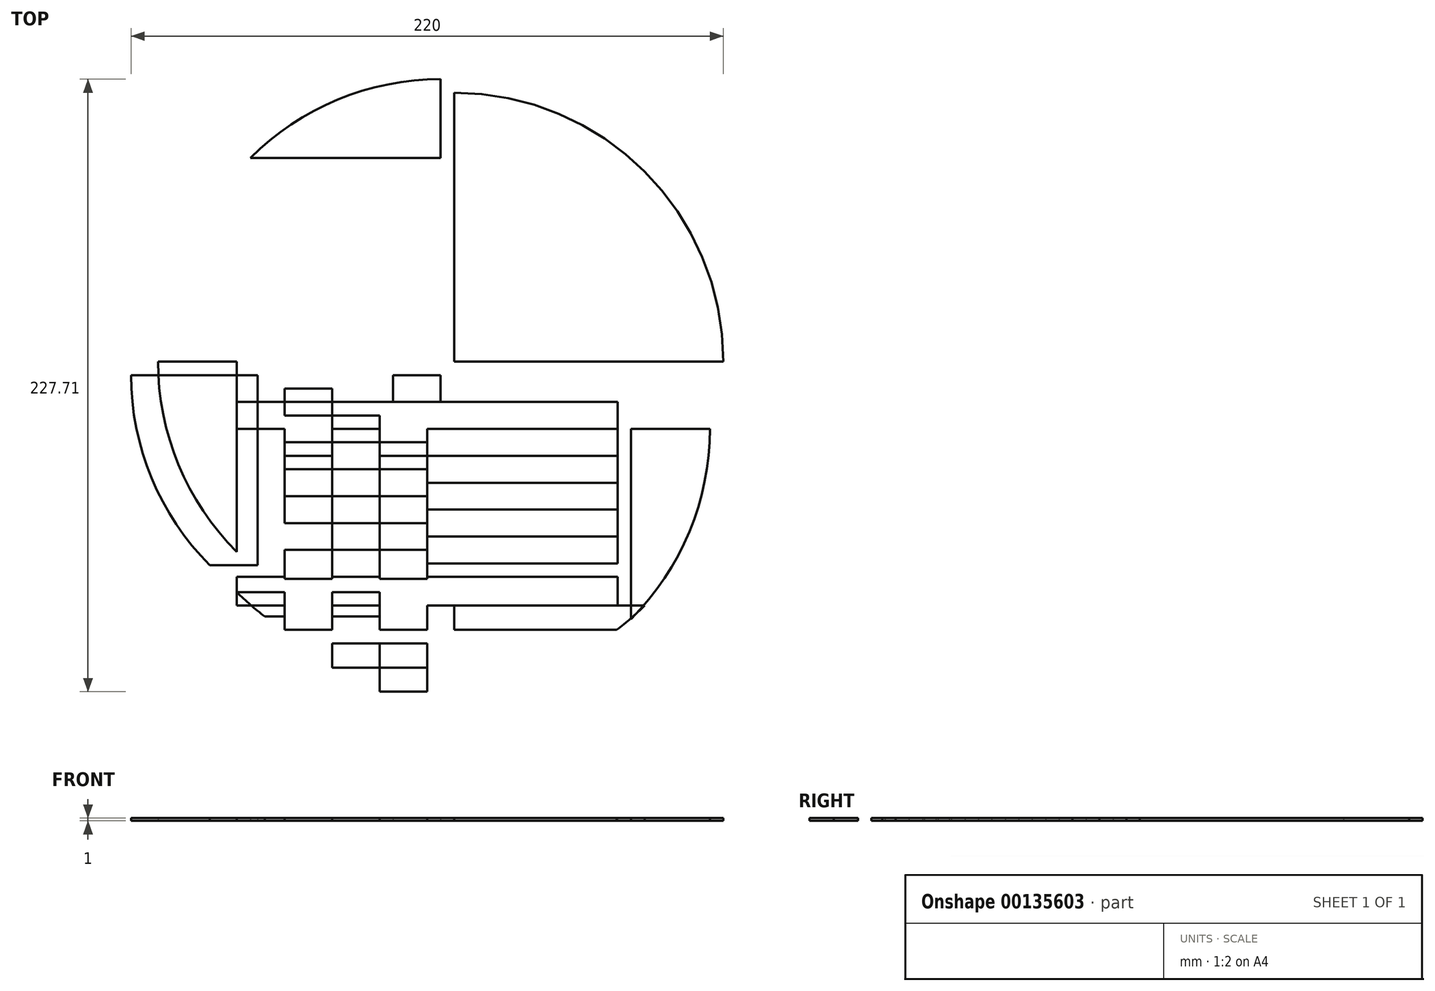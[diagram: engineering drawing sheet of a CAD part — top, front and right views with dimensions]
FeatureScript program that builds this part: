
annotation { "Feature Type Name" : "Feature", "Feature Type Description" : "" }
export const myFeature = defineFeature(function(context is Context, id is Id, definition is map)
    precondition{}
    {
        {
            assignVariable(context, id + "F0", {"name" : "d", "anyValue" : 5 * mm});
        }
        {
            var Q0;
            Q0=qCreatedBy(makeId("Top.planeOp"),FACE);
            var sketch = newSketch(context, id + "F1", { "sketchPlane" : qUnion([Q0])});
            skLineSegment(sketch, "E0.1", {"start": v(70.71, -70.71) * mm, "end": v(-70.71, -70.71) * mm});
            skLineSegment(sketch, "E0.2", {"start": v(-70.71, -70.71) * mm, "end": v(-70.71, 70.71) * mm});
            skLineSegment(sketch, "E1", {"start": v(70.71, 0) * mm, "end": v(-70.71, 0) * mm});
            skLineSegment(sketch, "E2", {"start": v(-14.1, -99) * mm, "end": v(14.1, -99) * mm});
            skArc(sketch, "E3", {"start": v(-14.1, -99) * mm, "mid": v(0, 100) * mm, "end": v(14.1, -99) * mm});
            skLineSegment(sketch, "E4", {"start": v(60.38, -79.71) * mm, "end": v(-60.38, -79.71) * mm});
            skLineSegment(sketch, "E5", {"start": v(46.16, -88.71) * mm, "end": v(-46.16, -88.71) * mm});
            skLineSegment(sketch, "E6", {"start": v(0, -70.71) * mm, "end": v(0, -99) * mm});
            skLineSegment(sketch, "E7", {"start": v(-70.71, 0) * mm, "end": v(-100, 0) * mm});
            skLineSegment(sketch, "E8", {"start": v(70.71, 0) * mm, "end": v(100, 0) * mm});
            skLineSegment(sketch, "E9", {"start": v(0, 70.71) * mm, "end": v(0, 100) * mm});
            skLineSegment(sketch, "E10", {"start": v(-70.71, -70.71) * mm, "end": v(-70.71, 0) * mm});
            skLineSegment(sketch, "E11", {"start": v(0, 70.71) * mm, "end": v(-70.71, 70.71) * mm});
            skLineSegment(sketch, "E12", {"start": v(70.71, 0) * mm, "end": v(70.71, -70.71) * mm});
            skLineSegment(sketch, "E13.0.1.0", {"start": v(70.71, -10) * mm, "end": v(-70.71, -10) * mm});
            skLineSegment(sketch, "E13.0.2.0", {"start": v(70.71, -20) * mm, "end": v(-70.71, -20) * mm});
            skLineSegment(sketch, "E13.0.3.0", {"start": v(70.71, -30) * mm, "end": v(-70.71, -30) * mm});
            skLineSegment(sketch, "E13.0.4.0", {"start": v(70.71, -40) * mm, "end": v(-70.71, -40) * mm});
            skLineSegment(sketch, "E13.0.5.0", {"start": v(70.71, -50) * mm, "end": v(-70.71, -50) * mm});
            skLineSegment(sketch, "E13.0.6.0", {"start": v(70.71, -60) * mm, "end": v(-70.71, -60) * mm});
            skLineSegment(sketch, "E13.direction1", {"start": v(-70.71, 0) * mm, "end": v(-45.71, 0) * mm, "construction": true});
            skLineSegment(sketch, "E13.direction2", {"start": v(-70.71, 0) * mm, "end": v(-70.71, -10) * mm, "construction": true});
            skLineSegment(sketch, "E14", {"start": v(0, 0) * mm, "end": v(0, 70.71) * mm});
            skLineSegment(sketch, "E15", {"start": v(0, 0) * mm, "end": v(0, -70.71) * mm});
            skLineSegment(sketch, "E16.1.0.0", {"start": v(-17.65, 0) * mm, "end": v(-17.65, -70.71) * mm});
            skLineSegment(sketch, "E16.2.0.0", {"start": v(-35.3, 0) * mm, "end": v(-35.3, -70.71) * mm});
            skLineSegment(sketch, "E16.3.0.0", {"start": v(-52.95, 0) * mm, "end": v(-52.95, -70.71) * mm});
            skLineSegment(sketch, "E16.direction1", {"start": v(0, -70.71) * mm, "end": v(-17.65, -70.71) * mm, "construction": true});
            skLineSegment(sketch, "E17", {"start": v(-35.3, -70.71) * mm, "end": v(-35.3, -88.71) * mm});
            skLineSegment(sketch, "E18", {"start": v(-52.95, -70.71) * mm, "end": v(-52.95, -79.71) * mm});
            skLineSegment(sketch, "E19", {"start": v(21.27, -97.71) * mm, "end": v(-21.27, -97.71) * mm});
            skLineSegment(sketch, "E20", {"start": v(-17.65, -70.71) * mm, "end": v(-17.65, -97.71) * mm});
            skSolve(sketch);
        }
        {
            var Q0;
            {var subQ0=sQuery(id+"F1.wireOp",EDGE,"E3");var subQ5=sQuery(id+"F1.wireOp",EDGE,"E4");var subQ6=makeQuery(id+"F1.imprint","INTERSECT",VERTEX,{"disambiguationData":[OD(0.0)],"derivedFrom":[subQ0,subQ5]});Q0=makeQuery(id+"F1.imprint","IMPRINT",FACE,{"disambiguationData":[TD([[makeQuery(id+"F1.imprint","IMPRINT",EDGE,{"disambiguationData":[TD([[subQ6,-1.0]])],"derivedFrom":subQ5}),-1.0]])]});}
            var Q1;
            {var subQ3=sQuery(id+"F1.wireOp",EDGE,"E18");Q1=makeQuery(id+"F1.imprint","IMPRINT",FACE,{"disambiguationData":[TD([[makeQuery(id+"F1.imprint","IMPRINT",EDGE,{"derivedFrom":subQ3}),-1.0]])]});}
            var Q2;
            {var subQ0=sQuery(id+"F1.wireOp",EDGE,"E20");var subQ5=sQuery(id+"F1.wireOp",EDGE,"E4");var subQ7=makeQuery(id+"F1.imprint","INTERSECT",VERTEX,{"derivedFrom":[subQ5,subQ0]});Q2=makeQuery(id+"F1.imprint","IMPRINT",FACE,{"disambiguationData":[TD([[makeQuery(id+"F1.imprint","IMPRINT",EDGE,{"disambiguationData":[TD([[subQ7,-1.0]])],"derivedFrom":subQ5}),-1.0]])]});}
            var Q3;
            {var subQ0=sQuery(id+"F1.wireOp",EDGE,"E15");var subQ5=sQuery(id+"F1.wireOp",EDGE,"E13.0.1.0");var subQ6=makeQuery(id+"F1.imprint","INTERSECT",VERTEX,{"derivedFrom":[subQ5,subQ0]});Q3=makeQuery(id+"F1.imprint","IMPRINT",FACE,{"disambiguationData":[TD([[makeQuery(id+"F1.imprint","IMPRINT",EDGE,{"disambiguationData":[TD([[subQ6,-1.0]])],"derivedFrom":subQ5}),-1.0]])]});}
            var Q4;
            {var subQ0=sQuery(id+"F1.wireOp",EDGE,"E16.2.0.0");var subQ1=sQuery(id+"F1.wireOp",EDGE,"E1");var subQ2=makeQuery(id+"F1.imprint","INTERSECT",VERTEX,{"derivedFrom":[subQ1,subQ0]});Q4=makeQuery(id+"F1.imprint","IMPRINT",FACE,{"disambiguationData":[TD([[makeQuery(id+"F1.imprint","IMPRINT",EDGE,{"disambiguationData":[TD([[subQ2,-1.0]])],"derivedFrom":subQ1}),1.0]])]});}
            var Q5;
            {var subQ0=sQuery(id+"F1.wireOp",EDGE,"E15");var subQ5=sQuery(id+"F1.wireOp",EDGE,"E13.0.1.0");var subQ6=makeQuery(id+"F1.imprint","INTERSECT",VERTEX,{"derivedFrom":[subQ5,subQ0]});Q5=makeQuery(id+"F1.imprint","IMPRINT",FACE,{"disambiguationData":[TD([[makeQuery(id+"F1.imprint","IMPRINT",EDGE,{"disambiguationData":[TD([[subQ6,-1.0]])],"derivedFrom":subQ5}),-1.0]])]});}
            var Q6;
            {var subQ0=sQuery(id+"F1.wireOp",EDGE,"E16.2.0.0");var subQ1=sQuery(id+"F1.wireOp",EDGE,"E1");var subQ2=makeQuery(id+"F1.imprint","INTERSECT",VERTEX,{"derivedFrom":[subQ1,subQ0]});Q6=makeQuery(id+"F1.imprint","IMPRINT",FACE,{"disambiguationData":[TD([[makeQuery(id+"F1.imprint","IMPRINT",EDGE,{"disambiguationData":[TD([[subQ2,-1.0]])],"derivedFrom":subQ1}),1.0]])]});}
            var Q7;
            {var subQ1=sQuery(id+"F1.wireOp",EDGE,"E8");Q7=makeQuery(id+"F1.imprint","IMPRINT",FACE,{"disambiguationData":[TD([[makeQuery(id+"F1.imprint","IMPRINT",EDGE,{"derivedFrom":subQ1}),1.0]])]});}
            var Q8;
            {var subQ0=sQuery(id+"F1.wireOp",EDGE,"E0.2");Q8=makeQuery(id+"F1.imprint","IMPRINT",FACE,{"disambiguationData":[TD([[makeQuery(id+"F1.imprint","IMPRINT",EDGE,{"derivedFrom":subQ0}),1.0]])]});}
            var Q9;
            {var subQ0=sQuery(id+"F1.wireOp",EDGE,"E15");var subQ5=sQuery(id+"F1.wireOp",EDGE,"E13.0.1.0");var subQ6=makeQuery(id+"F1.imprint","INTERSECT",VERTEX,{"derivedFrom":[subQ5,subQ0]});Q9=makeQuery(id+"F1.imprint","IMPRINT",FACE,{"disambiguationData":[TD([[makeQuery(id+"F1.imprint","IMPRINT",EDGE,{"disambiguationData":[TD([[subQ6,-1.0]])],"derivedFrom":subQ5}),-1.0]])]});}
            var Q10;
            {var subQ0=sQuery(id+"F1.wireOp",EDGE,"E16.2.0.0");var subQ1=sQuery(id+"F1.wireOp",EDGE,"E1");var subQ2=makeQuery(id+"F1.imprint","INTERSECT",VERTEX,{"derivedFrom":[subQ1,subQ0]});Q10=makeQuery(id+"F1.imprint","IMPRINT",FACE,{"disambiguationData":[TD([[makeQuery(id+"F1.imprint","IMPRINT",EDGE,{"disambiguationData":[TD([[subQ2,-1.0]])],"derivedFrom":subQ1}),1.0]])]});}
            var Q11;
            {var subQ0=sQuery(id+"F1.wireOp",EDGE,"E13.0.1.0");var subQ1=sQuery(id+"F1.wireOp",EDGE,"E10");var subQ2=makeQuery(id+"F1.imprint","INTERSECT",VERTEX,{"derivedFrom":[subQ1,subQ0]});Q11=makeQuery(id+"F1.imprint","IMPRINT",FACE,{"disambiguationData":[TD([[makeQuery(id+"F1.imprint","IMPRINT",EDGE,{"disambiguationData":[TD([[subQ2,1.0]])],"derivedFrom":subQ1}),-1.0]])]});}
            var Q12;
            {var subQ0=sQuery(id+"F1.wireOp",EDGE,"E16.2.0.0");var subQ1=sQuery(id+"F1.wireOp",EDGE,"E13.0.2.0");var subQ2=makeQuery(id+"F1.imprint","INTERSECT",VERTEX,{"derivedFrom":[subQ1,subQ0]});Q12=makeQuery(id+"F1.imprint","IMPRINT",FACE,{"disambiguationData":[TD([[makeQuery(id+"F1.imprint","IMPRINT",EDGE,{"disambiguationData":[TD([[subQ2,-1.0]])],"derivedFrom":subQ1}),1.0]])]});}
            var Q13;
            {var subQ0=sQuery(id+"F1.wireOp",EDGE,"E16.1.0.0");var subQ1=sQuery(id+"F1.wireOp",EDGE,"E13.0.1.0");var subQ2=makeQuery(id+"F1.imprint","INTERSECT",VERTEX,{"derivedFrom":[subQ1,subQ0]});Q13=makeQuery(id+"F1.imprint","IMPRINT",FACE,{"disambiguationData":[TD([[makeQuery(id+"F1.imprint","IMPRINT",EDGE,{"disambiguationData":[TD([[subQ2,-1.0]])],"derivedFrom":subQ1}),1.0]])]});}
            var Q14;
            {var subQ0=sQuery(id+"F1.wireOp",EDGE,"E15");var subQ1=sQuery(id+"F1.wireOp",EDGE,"E13.0.2.0");var subQ2=makeQuery(id+"F1.imprint","INTERSECT",VERTEX,{"derivedFrom":[subQ1,subQ0]});Q14=makeQuery(id+"F1.imprint","IMPRINT",FACE,{"disambiguationData":[TD([[makeQuery(id+"F1.imprint","IMPRINT",EDGE,{"disambiguationData":[TD([[subQ2,-1.0]])],"derivedFrom":subQ1}),1.0]])]});}
            var Q15;
            {var subQ0=sQuery(id+"F1.wireOp",EDGE,"E16.1.0.0");var subQ1=sQuery(id+"F1.wireOp",EDGE,"E13.0.3.0");var subQ2=makeQuery(id+"F1.imprint","INTERSECT",VERTEX,{"derivedFrom":[subQ1,subQ0]});Q15=makeQuery(id+"F1.imprint","IMPRINT",FACE,{"disambiguationData":[TD([[makeQuery(id+"F1.imprint","IMPRINT",EDGE,{"disambiguationData":[TD([[subQ2,-1.0]])],"derivedFrom":subQ1}),1.0]])]});}
            var Q16;
            {var subQ0=sQuery(id+"F1.wireOp",EDGE,"E13.0.3.0");var subQ1=sQuery(id+"F1.wireOp",EDGE,"E10");var subQ2=makeQuery(id+"F1.imprint","INTERSECT",VERTEX,{"derivedFrom":[subQ1,subQ0]});Q16=makeQuery(id+"F1.imprint","IMPRINT",FACE,{"disambiguationData":[TD([[makeQuery(id+"F1.imprint","IMPRINT",EDGE,{"disambiguationData":[TD([[subQ2,1.0]])],"derivedFrom":subQ1}),-1.0]])]});}
            var Q17;
            {var subQ0=sQuery(id+"F1.wireOp",EDGE,"E16.2.0.0");var subQ1=sQuery(id+"F1.wireOp",EDGE,"E13.0.4.0");var subQ2=makeQuery(id+"F1.imprint","INTERSECT",VERTEX,{"derivedFrom":[subQ1,subQ0]});Q17=makeQuery(id+"F1.imprint","IMPRINT",FACE,{"disambiguationData":[TD([[makeQuery(id+"F1.imprint","IMPRINT",EDGE,{"disambiguationData":[TD([[subQ2,-1.0]])],"derivedFrom":subQ1}),1.0]])]});}
            var Q18;
            {var subQ0=sQuery(id+"F1.wireOp",EDGE,"E15");var subQ1=sQuery(id+"F1.wireOp",EDGE,"E13.0.4.0");var subQ2=makeQuery(id+"F1.imprint","INTERSECT",VERTEX,{"derivedFrom":[subQ1,subQ0]});Q18=makeQuery(id+"F1.imprint","IMPRINT",FACE,{"disambiguationData":[TD([[makeQuery(id+"F1.imprint","IMPRINT",EDGE,{"disambiguationData":[TD([[subQ2,-1.0]])],"derivedFrom":subQ1}),1.0]])]});}
            var Q19;
            {var subQ0=sQuery(id+"F1.wireOp",EDGE,"E16.1.0.0");var subQ1=sQuery(id+"F1.wireOp",EDGE,"E13.0.5.0");var subQ2=makeQuery(id+"F1.imprint","INTERSECT",VERTEX,{"derivedFrom":[subQ1,subQ0]});Q19=makeQuery(id+"F1.imprint","IMPRINT",FACE,{"disambiguationData":[TD([[makeQuery(id+"F1.imprint","IMPRINT",EDGE,{"disambiguationData":[TD([[subQ2,-1.0]])],"derivedFrom":subQ1}),1.0]])]});}
            var Q20;
            {var subQ0=sQuery(id+"F1.wireOp",EDGE,"E16.2.0.0");var subQ5=sQuery(id+"F1.wireOp",EDGE,"E13.0.6.0");var subQ6=makeQuery(id+"F1.imprint","INTERSECT",VERTEX,{"derivedFrom":[subQ5,subQ0]});Q20=makeQuery(id+"F1.imprint","IMPRINT",FACE,{"disambiguationData":[TD([[makeQuery(id+"F1.imprint","IMPRINT",EDGE,{"disambiguationData":[TD([[subQ6,-1.0]])],"derivedFrom":subQ5}),1.0]])]});}
            var Q21;
            {var subQ0=sQuery(id+"F1.wireOp",EDGE,"E13.0.5.0");var subQ1=sQuery(id+"F1.wireOp",EDGE,"E10");var subQ2=makeQuery(id+"F1.imprint","INTERSECT",VERTEX,{"derivedFrom":[subQ1,subQ0]});Q21=makeQuery(id+"F1.imprint","IMPRINT",FACE,{"disambiguationData":[TD([[makeQuery(id+"F1.imprint","IMPRINT",EDGE,{"disambiguationData":[TD([[subQ2,1.0]])],"derivedFrom":subQ1}),-1.0]])]});}
            var Q22;
            {var subQ3=sQuery(id+"F1.wireOp",EDGE,"E18");Q22=makeQuery(id+"F1.imprint","IMPRINT",FACE,{"disambiguationData":[TD([[makeQuery(id+"F1.imprint","IMPRINT",EDGE,{"derivedFrom":subQ3}),-1.0]])]});}
            var Q23;
            {var subQ0=sQuery(id+"F1.wireOp",EDGE,"E13.0.1.0");var subQ1=sQuery(id+"F1.wireOp",EDGE,"E12");var subQ2=makeQuery(id+"F1.imprint","INTERSECT",VERTEX,{"derivedFrom":[subQ1,subQ0]});Q23=makeQuery(id+"F1.imprint","IMPRINT",FACE,{"disambiguationData":[TD([[makeQuery(id+"F1.imprint","IMPRINT",EDGE,{"disambiguationData":[TD([[subQ2,-1.0]])],"derivedFrom":subQ1}),-1.0]])]});}
            var Q24;
            {var subQ0=sQuery(id+"F1.wireOp",EDGE,"E13.0.3.0");var subQ1=sQuery(id+"F1.wireOp",EDGE,"E12");var subQ2=makeQuery(id+"F1.imprint","INTERSECT",VERTEX,{"derivedFrom":[subQ1,subQ0]});Q24=makeQuery(id+"F1.imprint","IMPRINT",FACE,{"disambiguationData":[TD([[makeQuery(id+"F1.imprint","IMPRINT",EDGE,{"disambiguationData":[TD([[subQ2,-1.0]])],"derivedFrom":subQ1}),-1.0]])]});}
            var Q25;
            {var subQ0=sQuery(id+"F1.wireOp",EDGE,"E13.0.5.0");var subQ1=sQuery(id+"F1.wireOp",EDGE,"E12");var subQ2=makeQuery(id+"F1.imprint","INTERSECT",VERTEX,{"derivedFrom":[subQ1,subQ0]});Q25=makeQuery(id+"F1.imprint","IMPRINT",FACE,{"disambiguationData":[TD([[makeQuery(id+"F1.imprint","IMPRINT",EDGE,{"disambiguationData":[TD([[subQ2,-1.0]])],"derivedFrom":subQ1}),-1.0]])]});}
            var Q26;
            {var subQ0=sQuery(id+"F1.wireOp",EDGE,"E15");var subQ5=sQuery(id+"F1.wireOp",EDGE,"E13.0.6.0");var subQ6=makeQuery(id+"F1.imprint","INTERSECT",VERTEX,{"derivedFrom":[subQ5,subQ0]});Q26=makeQuery(id+"F1.imprint","IMPRINT",FACE,{"disambiguationData":[TD([[makeQuery(id+"F1.imprint","IMPRINT",EDGE,{"disambiguationData":[TD([[subQ6,-1.0]])],"derivedFrom":subQ5}),1.0]])]});}
            var Q27;
            {var subQ0=sQuery(id+"F1.wireOp",EDGE,"E3");var subQ5=sQuery(id+"F1.wireOp",EDGE,"E4");var subQ6=makeQuery(id+"F1.imprint","INTERSECT",VERTEX,{"disambiguationData":[OD(0.0)],"derivedFrom":[subQ0,subQ5]});Q27=makeQuery(id+"F1.imprint","IMPRINT",FACE,{"disambiguationData":[TD([[makeQuery(id+"F1.imprint","IMPRINT",EDGE,{"disambiguationData":[TD([[subQ6,-1.0]])],"derivedFrom":subQ5}),-1.0]])]});}
            var Q28;
            {var subQ0=sQuery(id+"F1.wireOp",EDGE,"E6");var subQ1=sQuery(id+"F1.wireOp",EDGE,"E4");var subQ2=makeQuery(id+"F1.imprint","INTERSECT",VERTEX,{"derivedFrom":[subQ1,subQ0]});Q28=makeQuery(id+"F1.imprint","IMPRINT",FACE,{"disambiguationData":[TD([[makeQuery(id+"F1.imprint","IMPRINT",EDGE,{"disambiguationData":[TD([[subQ2,-1.0]])],"derivedFrom":subQ1}),1.0]])]});}
            var Q29;
            {var subQ1=sQuery(id+"F1.wireOp",EDGE,"E3");var subQ5=sQuery(id+"F1.wireOp",EDGE,"E5");var subQ6=makeQuery(id+"F1.imprint","INTERSECT",VERTEX,{"disambiguationData":[OD(1.0)],"derivedFrom":[subQ1,subQ5]});Q29=makeQuery(id+"F1.imprint","IMPRINT",FACE,{"disambiguationData":[TD([[makeQuery(id+"F1.imprint","IMPRINT",EDGE,{"disambiguationData":[TD([[subQ6,1.0]])],"derivedFrom":subQ1}),-1.0]])]});}
            var Q30;
            {var subQ0=sQuery(id+"F1.wireOp",EDGE,"E5");var subQ1=sQuery(id+"F1.wireOp",EDGE,"E3");var subQ2=makeQuery(id+"F1.imprint","INTERSECT",VERTEX,{"disambiguationData":[OD(0.0)],"derivedFrom":[subQ1,subQ0]});Q30=makeQuery(id+"F1.imprint","IMPRINT",FACE,{"disambiguationData":[TD([[makeQuery(id+"F1.imprint","IMPRINT",EDGE,{"disambiguationData":[TD([[subQ2,-1.0]])],"derivedFrom":subQ1}),-1.0]])]});}
            extrude(context, id + "F2", {"entities" : qUnion([Q0, Q1, Q2, Q3, Q4, Q5, Q6, Q7, Q8, Q9, Q10, Q11, Q12, Q13, Q14, Q15, Q16, Q17, Q18, Q19, Q20, Q21, Q22, Q23, Q24, Q25, Q26, Q27, Q28, Q29, Q30]), "depth" : 1 * mm});
        }
        {
            var Q0;
            {var subQ3=sQuery(id+"F1.wireOp",EDGE,"E8");Q0=makeQuery(id+"F1.imprint","IMPRINT",FACE,{"disambiguationData":[TD([[makeQuery(id+"F1.imprint","IMPRINT",EDGE,{"derivedFrom":subQ3}),-1.0]])]});}
            var Q1;
            {var subQ3=sQuery(id+"F1.wireOp",EDGE,"E7");Q1=makeQuery(id+"F1.imprint","IMPRINT",FACE,{"disambiguationData":[TD([[makeQuery(id+"F1.imprint","IMPRINT",EDGE,{"derivedFrom":subQ3}),1.0]])]});}
            var Q2;
            {var subQ5=sQuery(id+"F1.wireOp",EDGE,"E0.2");Q2=makeQuery(id+"F1.imprint","IMPRINT",FACE,{"disambiguationData":[TD([[makeQuery(id+"F1.imprint","IMPRINT",EDGE,{"derivedFrom":subQ5}),-1.0]])]});}
            var Q3;
            {var subQ1=sQuery(id+"F1.wireOp",EDGE,"E3");var subQ5=sQuery(id+"F1.wireOp",EDGE,"E4");var subQ6=makeQuery(id+"F1.imprint","INTERSECT",VERTEX,{"disambiguationData":[OD(1.0)],"derivedFrom":[subQ1,subQ5]});Q3=makeQuery(id+"F1.imprint","IMPRINT",FACE,{"disambiguationData":[TD([[makeQuery(id+"F1.imprint","IMPRINT",EDGE,{"disambiguationData":[TD([[subQ6,1.0]])],"derivedFrom":subQ1}),-1.0]])]});}
            var Q4;
            {var subQ1=sQuery(id+"F1.wireOp",EDGE,"E2");var subQ5=sQuery(id+"F1.wireOp",EDGE,"E3");var subQ6=makeQuery(id+"F1.imprint","INTERSECT",VERTEX,{"disambiguationData":[OD(0.0)],"derivedFrom":[subQ1,subQ5]});Q4=makeQuery(id+"F1.imprint","IMPRINT",FACE,{"disambiguationData":[TD([[makeQuery(id+"F1.imprint","IMPRINT",EDGE,{"disambiguationData":[TD([[subQ6,-1.0]])],"derivedFrom":subQ1}),1.0]])]});}
            extrude(context, id + "F3", {"entities" : qUnion([Q0, Q1, Q2, Q3, Q4]), "depth" : 1 * mm});
        }
        {
            var Q0;
            {var subQ0=sQuery(id+"F1.wireOp",EDGE,"E3");var subQ1=sQuery(id+"F1.wireOp",EDGE,"E2");var subQ2=makeQuery(id+"F1.imprint","INTERSECT",VERTEX,{"disambiguationData":[OD(1.0)],"derivedFrom":[subQ1,subQ0]});Q0=makeQuery(id+"F1.imprint","IMPRINT",FACE,{"disambiguationData":[TD([[makeQuery(id+"F1.imprint","IMPRINT",EDGE,{"disambiguationData":[TD([[subQ2,1.0]])],"derivedFrom":subQ1}),1.0]])]});}
            var Q1;
            {var subQ0=sQuery(id+"F1.wireOp",EDGE,"E6");var subQ1=sQuery(id+"F1.wireOp",EDGE,"E5");var subQ2=makeQuery(id+"F1.imprint","INTERSECT",VERTEX,{"derivedFrom":[subQ1,subQ0]});Q1=makeQuery(id+"F1.imprint","IMPRINT",FACE,{"disambiguationData":[TD([[makeQuery(id+"F1.imprint","IMPRINT",EDGE,{"disambiguationData":[TD([[subQ2,-1.0]])],"derivedFrom":subQ1}),1.0]])]});}
            var Q2;
            {var subQ0=sQuery(id+"F1.wireOp",EDGE,"E4");var subQ1=sQuery(id+"F1.wireOp",EDGE,"E3");var subQ2=makeQuery(id+"F1.imprint","INTERSECT",VERTEX,{"disambiguationData":[OD(0.0)],"derivedFrom":[subQ1,subQ0]});Q2=makeQuery(id+"F1.imprint","IMPRINT",FACE,{"disambiguationData":[TD([[makeQuery(id+"F1.imprint","IMPRINT",EDGE,{"disambiguationData":[TD([[subQ2,-1.0]])],"derivedFrom":subQ1}),-1.0]])]});}
            var Q3;
            {var subQ0=sQuery(id+"F1.wireOp",EDGE,"E20");var subQ1=sQuery(id+"F1.wireOp",EDGE,"E4");var subQ2=makeQuery(id+"F1.imprint","INTERSECT",VERTEX,{"derivedFrom":[subQ1,subQ0]});Q3=makeQuery(id+"F1.imprint","IMPRINT",FACE,{"disambiguationData":[TD([[makeQuery(id+"F1.imprint","IMPRINT",EDGE,{"disambiguationData":[TD([[subQ2,-1.0]])],"derivedFrom":subQ1}),1.0]])]});}
            var Q4;
            {var subQ0=sQuery(id+"F1.wireOp",EDGE,"E12");var subQ5=sQuery(id+"F1.wireOp",EDGE,"E13.0.6.0");var subQ6=makeQuery(id+"F1.imprint","INTERSECT",VERTEX,{"derivedFrom":[subQ0,subQ5]});Q4=makeQuery(id+"F1.imprint","IMPRINT",FACE,{"disambiguationData":[TD([[makeQuery(id+"F1.imprint","IMPRINT",EDGE,{"disambiguationData":[TD([[subQ6,-1.0]])],"derivedFrom":subQ5}),1.0]])]});}
            var Q5;
            {var subQ0=sQuery(id+"F1.wireOp",EDGE,"E6");var subQ5=sQuery(id+"F1.wireOp",EDGE,"E4");var subQ6=makeQuery(id+"F1.imprint","INTERSECT",VERTEX,{"derivedFrom":[subQ5,subQ0]});Q5=makeQuery(id+"F1.imprint","IMPRINT",FACE,{"disambiguationData":[TD([[makeQuery(id+"F1.imprint","IMPRINT",EDGE,{"disambiguationData":[TD([[subQ6,-1.0]])],"derivedFrom":subQ5}),-1.0]])]});}
            var Q6;
            {var subQ0=sQuery(id+"F1.wireOp",EDGE,"E15");var subQ1=sQuery(id+"F1.wireOp",EDGE,"E13.0.5.0");var subQ2=makeQuery(id+"F1.imprint","INTERSECT",VERTEX,{"derivedFrom":[subQ1,subQ0]});Q6=makeQuery(id+"F1.imprint","IMPRINT",FACE,{"disambiguationData":[TD([[makeQuery(id+"F1.imprint","IMPRINT",EDGE,{"disambiguationData":[TD([[subQ2,-1.0]])],"derivedFrom":subQ1}),1.0]])]});}
            var Q7;
            {var subQ3=sQuery(id+"F1.wireOp",EDGE,"E18");Q7=makeQuery(id+"F1.imprint","IMPRINT",FACE,{"disambiguationData":[TD([[makeQuery(id+"F1.imprint","IMPRINT",EDGE,{"derivedFrom":subQ3}),1.0]])]});}
            var Q8;
            {var subQ0=sQuery(id+"F1.wireOp",EDGE,"E16.1.0.0");var subQ5=sQuery(id+"F1.wireOp",EDGE,"E13.0.6.0");var subQ6=makeQuery(id+"F1.imprint","INTERSECT",VERTEX,{"derivedFrom":[subQ5,subQ0]});Q8=makeQuery(id+"F1.imprint","IMPRINT",FACE,{"disambiguationData":[TD([[makeQuery(id+"F1.imprint","IMPRINT",EDGE,{"disambiguationData":[TD([[subQ6,-1.0]])],"derivedFrom":subQ5}),1.0]])]});}
            var Q9;
            {var subQ0=sQuery(id+"F1.wireOp",EDGE,"E10");var subQ5=sQuery(id+"F1.wireOp",EDGE,"E13.0.6.0");var subQ6=makeQuery(id+"F1.imprint","INTERSECT",VERTEX,{"derivedFrom":[subQ0,subQ5]});Q9=makeQuery(id+"F1.imprint","IMPRINT",FACE,{"disambiguationData":[TD([[makeQuery(id+"F1.imprint","IMPRINT",EDGE,{"disambiguationData":[TD([[subQ6,1.0]])],"derivedFrom":subQ5}),1.0]])]});}
            var Q10;
            {var subQ0=sQuery(id+"F1.wireOp",EDGE,"E16.2.0.0");var subQ1=sQuery(id+"F1.wireOp",EDGE,"E13.0.5.0");var subQ2=makeQuery(id+"F1.imprint","INTERSECT",VERTEX,{"derivedFrom":[subQ1,subQ0]});Q10=makeQuery(id+"F1.imprint","IMPRINT",FACE,{"disambiguationData":[TD([[makeQuery(id+"F1.imprint","IMPRINT",EDGE,{"disambiguationData":[TD([[subQ2,-1.0]])],"derivedFrom":subQ1}),1.0]])]});}
            var Q11;
            {var subQ0=sQuery(id+"F1.wireOp",EDGE,"E13.0.4.0");var subQ1=sQuery(id+"F1.wireOp",EDGE,"E10");var subQ2=makeQuery(id+"F1.imprint","INTERSECT",VERTEX,{"derivedFrom":[subQ1,subQ0]});Q11=makeQuery(id+"F1.imprint","IMPRINT",FACE,{"disambiguationData":[TD([[makeQuery(id+"F1.imprint","IMPRINT",EDGE,{"disambiguationData":[TD([[subQ2,1.0]])],"derivedFrom":subQ1}),-1.0]])]});}
            var Q12;
            {var subQ0=sQuery(id+"F1.wireOp",EDGE,"E16.1.0.0");var subQ1=sQuery(id+"F1.wireOp",EDGE,"E13.0.4.0");var subQ2=makeQuery(id+"F1.imprint","INTERSECT",VERTEX,{"derivedFrom":[subQ1,subQ0]});Q12=makeQuery(id+"F1.imprint","IMPRINT",FACE,{"disambiguationData":[TD([[makeQuery(id+"F1.imprint","IMPRINT",EDGE,{"disambiguationData":[TD([[subQ2,-1.0]])],"derivedFrom":subQ1}),1.0]])]});}
            var Q13;
            {var subQ0=sQuery(id+"F1.wireOp",EDGE,"E16.2.0.0");var subQ1=sQuery(id+"F1.wireOp",EDGE,"E13.0.3.0");var subQ2=makeQuery(id+"F1.imprint","INTERSECT",VERTEX,{"derivedFrom":[subQ1,subQ0]});Q13=makeQuery(id+"F1.imprint","IMPRINT",FACE,{"disambiguationData":[TD([[makeQuery(id+"F1.imprint","IMPRINT",EDGE,{"disambiguationData":[TD([[subQ2,-1.0]])],"derivedFrom":subQ1}),1.0]])]});}
            var Q14;
            {var subQ0=sQuery(id+"F1.wireOp",EDGE,"E16.1.0.0");var subQ1=sQuery(id+"F1.wireOp",EDGE,"E13.0.2.0");var subQ2=makeQuery(id+"F1.imprint","INTERSECT",VERTEX,{"derivedFrom":[subQ1,subQ0]});Q14=makeQuery(id+"F1.imprint","IMPRINT",FACE,{"disambiguationData":[TD([[makeQuery(id+"F1.imprint","IMPRINT",EDGE,{"disambiguationData":[TD([[subQ2,-1.0]])],"derivedFrom":subQ1}),1.0]])]});}
            var Q15;
            {var subQ0=sQuery(id+"F1.wireOp",EDGE,"E15");var subQ1=sQuery(id+"F1.wireOp",EDGE,"E13.0.3.0");var subQ2=makeQuery(id+"F1.imprint","INTERSECT",VERTEX,{"derivedFrom":[subQ1,subQ0]});Q15=makeQuery(id+"F1.imprint","IMPRINT",FACE,{"disambiguationData":[TD([[makeQuery(id+"F1.imprint","IMPRINT",EDGE,{"disambiguationData":[TD([[subQ2,-1.0]])],"derivedFrom":subQ1}),1.0]])]});}
            var Q16;
            {var subQ0=sQuery(id+"F1.wireOp",EDGE,"E15");var subQ1=sQuery(id+"F1.wireOp",EDGE,"E13.0.1.0");var subQ2=makeQuery(id+"F1.imprint","INTERSECT",VERTEX,{"derivedFrom":[subQ1,subQ0]});Q16=makeQuery(id+"F1.imprint","IMPRINT",FACE,{"disambiguationData":[TD([[makeQuery(id+"F1.imprint","IMPRINT",EDGE,{"disambiguationData":[TD([[subQ2,-1.0]])],"derivedFrom":subQ1}),1.0]])]});}
            var Q17;
            {var subQ0=sQuery(id+"F1.wireOp",EDGE,"E16.1.0.0");var subQ1=sQuery(id+"F1.wireOp",EDGE,"E1");var subQ2=makeQuery(id+"F1.imprint","INTERSECT",VERTEX,{"derivedFrom":[subQ1,subQ0]});Q17=makeQuery(id+"F1.imprint","IMPRINT",FACE,{"disambiguationData":[TD([[makeQuery(id+"F1.imprint","IMPRINT",EDGE,{"disambiguationData":[TD([[subQ2,-1.0]])],"derivedFrom":subQ1}),1.0]])]});}
            var Q18;
            {var subQ0=sQuery(id+"F1.wireOp",EDGE,"E16.2.0.0");var subQ1=sQuery(id+"F1.wireOp",EDGE,"E13.0.1.0");var subQ2=makeQuery(id+"F1.imprint","INTERSECT",VERTEX,{"derivedFrom":[subQ1,subQ0]});Q18=makeQuery(id+"F1.imprint","IMPRINT",FACE,{"disambiguationData":[TD([[makeQuery(id+"F1.imprint","IMPRINT",EDGE,{"disambiguationData":[TD([[subQ2,-1.0]])],"derivedFrom":subQ1}),1.0]])]});}
            var Q19;
            {var subQ0=sQuery(id+"F1.wireOp",EDGE,"E13.0.2.0");var subQ1=sQuery(id+"F1.wireOp",EDGE,"E10");var subQ2=makeQuery(id+"F1.imprint","INTERSECT",VERTEX,{"derivedFrom":[subQ1,subQ0]});Q19=makeQuery(id+"F1.imprint","IMPRINT",FACE,{"disambiguationData":[TD([[makeQuery(id+"F1.imprint","IMPRINT",EDGE,{"disambiguationData":[TD([[subQ2,1.0]])],"derivedFrom":subQ1}),-1.0]])]});}
            var Q20;
            {var subQ0=sQuery(id+"F1.wireOp",EDGE,"E10");var subQ5=sQuery(id+"F1.wireOp",EDGE,"E13.0.1.0");var subQ6=makeQuery(id+"F1.imprint","INTERSECT",VERTEX,{"derivedFrom":[subQ0,subQ5]});Q20=makeQuery(id+"F1.imprint","IMPRINT",FACE,{"disambiguationData":[TD([[makeQuery(id+"F1.imprint","IMPRINT",EDGE,{"disambiguationData":[TD([[subQ6,1.0]])],"derivedFrom":subQ5}),-1.0]])]});}
            var Q21;
            {var subQ0=sQuery(id+"F1.wireOp",EDGE,"E12");var subQ5=sQuery(id+"F1.wireOp",EDGE,"E13.0.1.0");var subQ6=makeQuery(id+"F1.imprint","INTERSECT",VERTEX,{"derivedFrom":[subQ0,subQ5]});Q21=makeQuery(id+"F1.imprint","IMPRINT",FACE,{"disambiguationData":[TD([[makeQuery(id+"F1.imprint","IMPRINT",EDGE,{"disambiguationData":[TD([[subQ6,-1.0]])],"derivedFrom":subQ5}),-1.0]])]});}
            var Q22;
            {var subQ0=sQuery(id+"F1.wireOp",EDGE,"E13.0.2.0");var subQ1=sQuery(id+"F1.wireOp",EDGE,"E12");var subQ2=makeQuery(id+"F1.imprint","INTERSECT",VERTEX,{"derivedFrom":[subQ1,subQ0]});Q22=makeQuery(id+"F1.imprint","IMPRINT",FACE,{"disambiguationData":[TD([[makeQuery(id+"F1.imprint","IMPRINT",EDGE,{"disambiguationData":[TD([[subQ2,-1.0]])],"derivedFrom":subQ1}),-1.0]])]});}
            var Q23;
            {var subQ0=sQuery(id+"F1.wireOp",EDGE,"E13.0.4.0");var subQ1=sQuery(id+"F1.wireOp",EDGE,"E12");var subQ2=makeQuery(id+"F1.imprint","INTERSECT",VERTEX,{"derivedFrom":[subQ1,subQ0]});Q23=makeQuery(id+"F1.imprint","IMPRINT",FACE,{"disambiguationData":[TD([[makeQuery(id+"F1.imprint","IMPRINT",EDGE,{"disambiguationData":[TD([[subQ2,-1.0]])],"derivedFrom":subQ1}),-1.0]])]});}
            var Q24;
            {var subQ2=sQuery(id+"F1.wireOp",EDGE,"E9");Q24=makeQuery(id+"F1.imprint","IMPRINT",FACE,{"disambiguationData":[TD([[makeQuery(id+"F1.imprint","IMPRINT",EDGE,{"derivedFrom":subQ2}),1.0]])]});}
            extrude(context, id + "F4", {"entities" : qUnion([Q0, Q1, Q2, Q3, Q4, Q5, Q6, Q7, Q8, Q9, Q10, Q11, Q12, Q13, Q14, Q15, Q16, Q17, Q18, Q19, Q20, Q21, Q22, Q23, Q24]), "depth" : 1 * mm});
        }
        {
            var Q0;
            Q0=makeQuery(id+"F3.opExtrude","SWEPT_BODY",BODY,{"disambiguationData":[OSD([sQuery(id+"F1.wireOp",EDGE,"E0.2"),sQuery(id+"F1.wireOp",EDGE,"E1"),sQuery(id+"F1.wireOp",EDGE,"E11"),sQuery(id+"F1.wireOp",EDGE,"E14")])]});
            var Q1;
            Q1=makeQuery(id+"F2.opExtrude","SWEPT_BODY",BODY,{"disambiguationData":[OSD([sQuery(id+"F1.wireOp",EDGE,"E0.2"),sQuery(id+"F1.wireOp",EDGE,"E3"),sQuery(id+"F1.wireOp",EDGE,"E7")])]});
            var Q2;
            Q2=makeQuery(id+"F4.opExtrude","SWEPT_BODY",BODY,{"disambiguationData":[OSD([sQuery(id+"F1.wireOp",EDGE,"E3"),sQuery(id+"F1.wireOp",EDGE,"E9"),sQuery(id+"F1.wireOp",EDGE,"E11")])]});
            var Q3;
            Q3=sQuery(id+"F1.wireOp",EDGE,"Lgyj7vdr-Zl23-fVqB-5WY6-XuLikOYo5ZJ7");
            transform(context, id + "F5", {"entities" : qUnion([Q0, Q1, Q2]), "transformType" : TransformType.TRANSLATION_3D, "dx" : -getVariable(context, 'd'), "dy" : 0 * mm, "dz" : 0 * mm, "makeCopy" : false});
        }
        {
            var Q0;
            Q0=makeQuery(id+"F2.opExtrude","SWEPT_BODY",BODY,{"disambiguationData":[OSD([sQuery(id+"F1.wireOp",EDGE,"E1"),sQuery(id+"F1.wireOp",EDGE,"E13.0.1.0"),sQuery(id+"F1.wireOp",EDGE,"E15"),sQuery(id+"F1.wireOp",EDGE,"E16.1.0.0")])]});
            var Q1;
            Q1=makeQuery(id+"F2.opExtrude","SWEPT_BODY",BODY,{"disambiguationData":[OSD([sQuery(id+"F1.wireOp",EDGE,"E1"),sQuery(id+"F1.wireOp",EDGE,"E13.0.1.0"),sQuery(id+"F1.wireOp",EDGE,"E16.2.0.0"),sQuery(id+"F1.wireOp",EDGE,"E16.3.0.0")])]});
            var Q2;
            Q2=makeQuery(id+"F3.opExtrude","SWEPT_BODY",BODY,{"disambiguationData":[OSD([sQuery(id+"F1.wireOp",EDGE,"E3"),sQuery(id+"F1.wireOp",EDGE,"E7"),sQuery(id+"F1.wireOp",EDGE,"E10")])]});
            var Q3;
            Q3=makeQuery(id+"F3.opExtrude","SWEPT_BODY",BODY,{"disambiguationData":[OSD([sQuery(id+"F1.wireOp",EDGE,"E3"),sQuery(id+"F1.wireOp",EDGE,"E4"),sQuery(id+"F1.wireOp",EDGE,"E5"),sQuery(id+"F1.wireOp",EDGE,"E17")])]});
            var Q4;
            Q4=makeQuery(id+"F2.opExtrude","SWEPT_BODY",BODY,{"disambiguationData":[OSD([sQuery(id+"F1.wireOp",EDGE,"E13.0.3.0"),sQuery(id+"F1.wireOp",EDGE,"E13.0.4.0"),sQuery(id+"F1.wireOp",EDGE,"E16.1.0.0"),sQuery(id+"F1.wireOp",EDGE,"E16.2.0.0")])]});
            var Q5;
            Q5=makeQuery(id+"F2.opExtrude","SWEPT_BODY",BODY,{"disambiguationData":[OSD([sQuery(id+"F1.wireOp",EDGE,"E13.0.4.0"),sQuery(id+"F1.wireOp",EDGE,"E13.0.5.0"),sQuery(id+"F1.wireOp",EDGE,"E15"),sQuery(id+"F1.wireOp",EDGE,"E16.1.0.0")])]});
            var Q6;
            Q6=makeQuery(id+"F2.opExtrude","SWEPT_BODY",BODY,{"disambiguationData":[OSD([sQuery(id+"F1.wireOp",EDGE,"E13.0.4.0"),sQuery(id+"F1.wireOp",EDGE,"E13.0.5.0"),sQuery(id+"F1.wireOp",EDGE,"E16.2.0.0"),sQuery(id+"F1.wireOp",EDGE,"E16.3.0.0")])]});
            var Q7;
            Q7=makeQuery(id+"F2.opExtrude","SWEPT_BODY",BODY,{"disambiguationData":[OSD([sQuery(id+"F1.wireOp",EDGE,"E13.0.5.0"),sQuery(id+"F1.wireOp",EDGE,"E13.0.6.0"),sQuery(id+"F1.wireOp",EDGE,"E16.1.0.0"),sQuery(id+"F1.wireOp",EDGE,"E16.2.0.0")])]});
            var Q8;
            Q8=makeQuery(id+"F2.opExtrude","SWEPT_BODY",BODY,{"disambiguationData":[OSD([sQuery(id+"F1.wireOp",EDGE,"E3"),sQuery(id+"F1.wireOp",EDGE,"E5"),sQuery(id+"F1.wireOp",EDGE,"E19"),sQuery(id+"F1.wireOp",EDGE,"E20")])]});
            var Q9;
            Q9=makeQuery(id+"F3.opExtrude","SWEPT_BODY",BODY,{"disambiguationData":[OSD([sQuery(id+"F1.wireOp",EDGE,"E2"),sQuery(id+"F1.wireOp",EDGE,"E3"),sQuery(id+"F1.wireOp",EDGE,"E6"),sQuery(id+"F1.wireOp",EDGE,"E19")])]});
            var Q10;
            Q10=makeQuery(id+"F4.opExtrude","SWEPT_BODY",BODY,{"disambiguationData":[OSD([sQuery(id+"F1.wireOp",EDGE,"E10"),sQuery(id+"F1.wireOp",EDGE,"E13.0.4.0"),sQuery(id+"F1.wireOp",EDGE,"E13.0.5.0"),sQuery(id+"F1.wireOp",EDGE,"E16.3.0.0")])]});
            var Q11;
            Q11=makeQuery(id+"F4.opExtrude","SWEPT_BODY",BODY,{"disambiguationData":[OSD([sQuery(id+"F1.wireOp",EDGE,"E13.0.5.0"),sQuery(id+"F1.wireOp",EDGE,"E13.0.6.0"),sQuery(id+"F1.wireOp",EDGE,"E16.2.0.0"),sQuery(id+"F1.wireOp",EDGE,"E16.3.0.0")])]});
            var Q12;
            Q12=makeQuery(id+"F4.opExtrude","SWEPT_BODY",BODY,{"disambiguationData":[OSD([sQuery(id+"F1.wireOp",EDGE,"E13.0.5.0"),sQuery(id+"F1.wireOp",EDGE,"E13.0.6.0"),sQuery(id+"F1.wireOp",EDGE,"E15"),sQuery(id+"F1.wireOp",EDGE,"E16.1.0.0")])]});
            var Q13;
            Q13=makeQuery(id+"F4.opExtrude","SWEPT_BODY",BODY,{"disambiguationData":[OSD([sQuery(id+"F1.wireOp",EDGE,"E13.0.4.0"),sQuery(id+"F1.wireOp",EDGE,"E13.0.5.0"),sQuery(id+"F1.wireOp",EDGE,"E16.1.0.0"),sQuery(id+"F1.wireOp",EDGE,"E16.2.0.0")])]});
            var Q14;
            Q14=makeQuery(id+"F4.opExtrude","SWEPT_BODY",BODY,{"disambiguationData":[OSD([sQuery(id+"F1.wireOp",EDGE,"E13.0.3.0"),sQuery(id+"F1.wireOp",EDGE,"E13.0.4.0"),sQuery(id+"F1.wireOp",EDGE,"E16.2.0.0"),sQuery(id+"F1.wireOp",EDGE,"E16.3.0.0")])]});
            var Q15;
            Q15=makeQuery(id+"F4.opExtrude","SWEPT_BODY",BODY,{"disambiguationData":[OSD([sQuery(id+"F1.wireOp",EDGE,"E13.0.3.0"),sQuery(id+"F1.wireOp",EDGE,"E13.0.4.0"),sQuery(id+"F1.wireOp",EDGE,"E15"),sQuery(id+"F1.wireOp",EDGE,"E16.1.0.0")])]});
            var Q16;
            Q16=makeQuery(id+"F4.opExtrude","SWEPT_BODY",BODY,{"disambiguationData":[OSD([sQuery(id+"F1.wireOp",EDGE,"E13.0.2.0"),sQuery(id+"F1.wireOp",EDGE,"E13.0.3.0"),sQuery(id+"F1.wireOp",EDGE,"E16.1.0.0"),sQuery(id+"F1.wireOp",EDGE,"E16.2.0.0")])]});
            var Q17;
            Q17=makeQuery(id+"F4.opExtrude","SWEPT_BODY",BODY,{"disambiguationData":[OSD([sQuery(id+"F1.wireOp",EDGE,"E13.0.1.0"),sQuery(id+"F1.wireOp",EDGE,"E13.0.2.0"),sQuery(id+"F1.wireOp",EDGE,"E16.2.0.0"),sQuery(id+"F1.wireOp",EDGE,"E16.3.0.0")])]});
            var Q18;
            Q18=makeQuery(id+"F4.opExtrude","SWEPT_BODY",BODY,{"disambiguationData":[OSD([sQuery(id+"F1.wireOp",EDGE,"E13.0.1.0"),sQuery(id+"F1.wireOp",EDGE,"E13.0.2.0"),sQuery(id+"F1.wireOp",EDGE,"E15"),sQuery(id+"F1.wireOp",EDGE,"E16.1.0.0")])]});
            var Q19;
            Q19=makeQuery(id+"F4.opExtrude","SWEPT_BODY",BODY,{"disambiguationData":[OSD([sQuery(id+"F1.wireOp",EDGE,"E5"),sQuery(id+"F1.wireOp",EDGE,"E6"),sQuery(id+"F1.wireOp",EDGE,"E19"),sQuery(id+"F1.wireOp",EDGE,"E20")])]});
            var Q20;
            Q20=makeQuery(id+"F4.opExtrude","SWEPT_BODY",BODY,{"disambiguationData":[OSD([sQuery(id+"F1.wireOp",EDGE,"E10"),sQuery(id+"F1.wireOp",EDGE,"E13.0.2.0"),sQuery(id+"F1.wireOp",EDGE,"E13.0.3.0"),sQuery(id+"F1.wireOp",EDGE,"E16.3.0.0")])]});
            var Q21;
            Q21=makeQuery(id+"F4.opExtrude","SWEPT_BODY",BODY,{"disambiguationData":[OSD([sQuery(id+"F1.wireOp",EDGE,"E4"),sQuery(id+"F1.wireOp",EDGE,"E5"),sQuery(id+"F1.wireOp",EDGE,"E17"),sQuery(id+"F1.wireOp",EDGE,"E20")])]});
            var Q22;
            Q22=makeQuery(id+"F4.opExtrude","SWEPT_BODY",BODY,{"disambiguationData":[OSD([sQuery(id+"F1.wireOp",EDGE,"E1"),sQuery(id+"F1.wireOp",EDGE,"E10"),sQuery(id+"F1.wireOp",EDGE,"E13.0.1.0"),sQuery(id+"F1.wireOp",EDGE,"E16.3.0.0")])]});
            var Q23;
            Q23=makeQuery(id+"F4.opExtrude","SWEPT_BODY",BODY,{"disambiguationData":[OSD([sQuery(id+"F1.wireOp",EDGE,"E1"),sQuery(id+"F1.wireOp",EDGE,"E13.0.1.0"),sQuery(id+"F1.wireOp",EDGE,"E16.1.0.0"),sQuery(id+"F1.wireOp",EDGE,"E16.2.0.0")])]});
            var Q24;
            Q24=makeQuery(id+"F4.opExtrude","SWEPT_BODY",BODY,{"disambiguationData":[OSD([sQuery(id+"F1.wireOp",EDGE,"E0.1"),sQuery(id+"F1.wireOp",EDGE,"E10"),sQuery(id+"F1.wireOp",EDGE,"E13.0.6.0"),sQuery(id+"F1.wireOp",EDGE,"E16.3.0.0")])]});
            var Q25;
            Q25=makeQuery(id+"F4.opExtrude","SWEPT_BODY",BODY,{"disambiguationData":[OSD([sQuery(id+"F1.wireOp",EDGE,"E0.1"),sQuery(id+"F1.wireOp",EDGE,"E4"),sQuery(id+"F1.wireOp",EDGE,"E17"),sQuery(id+"F1.wireOp",EDGE,"E18")])]});
            var Q26;
            Q26=makeQuery(id+"F4.opExtrude","SWEPT_BODY",BODY,{"disambiguationData":[OSD([sQuery(id+"F1.wireOp",EDGE,"E0.1"),sQuery(id+"F1.wireOp",EDGE,"E4"),sQuery(id+"F1.wireOp",EDGE,"E6"),sQuery(id+"F1.wireOp",EDGE,"E20")])]});
            var Q27;
            Q27=makeQuery(id+"F4.opExtrude","SWEPT_BODY",BODY,{"disambiguationData":[OSD([sQuery(id+"F1.wireOp",EDGE,"E0.1"),sQuery(id+"F1.wireOp",EDGE,"E13.0.6.0"),sQuery(id+"F1.wireOp",EDGE,"E16.1.0.0"),sQuery(id+"F1.wireOp",EDGE,"E16.2.0.0")])]});
            var Q28;
            Q28=makeQuery(id+"F2.opExtrude","SWEPT_BODY",BODY,{"disambiguationData":[OSD([sQuery(id+"F1.wireOp",EDGE,"E13.0.2.0"),sQuery(id+"F1.wireOp",EDGE,"E13.0.3.0"),sQuery(id+"F1.wireOp",EDGE,"E16.2.0.0"),sQuery(id+"F1.wireOp",EDGE,"E16.3.0.0")])]});
            var Q29;
            Q29=makeQuery(id+"F2.opExtrude","SWEPT_BODY",BODY,{"disambiguationData":[OSD([sQuery(id+"F1.wireOp",EDGE,"E13.0.2.0"),sQuery(id+"F1.wireOp",EDGE,"E13.0.3.0"),sQuery(id+"F1.wireOp",EDGE,"E15"),sQuery(id+"F1.wireOp",EDGE,"E16.1.0.0")])]});
            var Q30;
            Q30=makeQuery(id+"F2.opExtrude","SWEPT_BODY",BODY,{"disambiguationData":[OSD([sQuery(id+"F1.wireOp",EDGE,"E13.0.1.0"),sQuery(id+"F1.wireOp",EDGE,"E13.0.2.0"),sQuery(id+"F1.wireOp",EDGE,"E16.1.0.0"),sQuery(id+"F1.wireOp",EDGE,"E16.2.0.0")])]});
            var Q31;
            Q31=makeQuery(id+"F2.opExtrude","SWEPT_BODY",BODY,{"disambiguationData":[OSD([sQuery(id+"F1.wireOp",EDGE,"E10"),sQuery(id+"F1.wireOp",EDGE,"E13.0.1.0"),sQuery(id+"F1.wireOp",EDGE,"E13.0.2.0"),sQuery(id+"F1.wireOp",EDGE,"E16.3.0.0")])]});
            var Q32;
            Q32=makeQuery(id+"F2.opExtrude","SWEPT_BODY",BODY,{"disambiguationData":[OSD([sQuery(id+"F1.wireOp",EDGE,"E10"),sQuery(id+"F1.wireOp",EDGE,"E13.0.3.0"),sQuery(id+"F1.wireOp",EDGE,"E13.0.4.0"),sQuery(id+"F1.wireOp",EDGE,"E16.3.0.0")])]});
            var Q33;
            Q33=makeQuery(id+"F2.opExtrude","SWEPT_BODY",BODY,{"disambiguationData":[OSD([sQuery(id+"F1.wireOp",EDGE,"E10"),sQuery(id+"F1.wireOp",EDGE,"E13.0.5.0"),sQuery(id+"F1.wireOp",EDGE,"E13.0.6.0"),sQuery(id+"F1.wireOp",EDGE,"E16.3.0.0")])]});
            var Q34;
            Q34=makeQuery(id+"F2.opExtrude","SWEPT_BODY",BODY,{"disambiguationData":[OSD([sQuery(id+"F1.wireOp",EDGE,"E4"),sQuery(id+"F1.wireOp",EDGE,"E5"),sQuery(id+"F1.wireOp",EDGE,"E6"),sQuery(id+"F1.wireOp",EDGE,"E20")])]});
            var Q35;
            Q35=makeQuery(id+"F2.opExtrude","SWEPT_BODY",BODY,{"disambiguationData":[OSD([sQuery(id+"F1.wireOp",EDGE,"E0.1"),sQuery(id+"F1.wireOp",EDGE,"E3"),sQuery(id+"F1.wireOp",EDGE,"E4"),sQuery(id+"F1.wireOp",EDGE,"E18")])]});
            var Q36;
            Q36=makeQuery(id+"F2.opExtrude","SWEPT_BODY",BODY,{"disambiguationData":[OSD([sQuery(id+"F1.wireOp",EDGE,"E0.1"),sQuery(id+"F1.wireOp",EDGE,"E13.0.6.0"),sQuery(id+"F1.wireOp",EDGE,"E16.2.0.0"),sQuery(id+"F1.wireOp",EDGE,"E16.3.0.0")])]});
            var Q37;
            Q37=makeQuery(id+"F2.opExtrude","SWEPT_BODY",BODY,{"disambiguationData":[OSD([sQuery(id+"F1.wireOp",EDGE,"E0.1"),sQuery(id+"F1.wireOp",EDGE,"E4"),sQuery(id+"F1.wireOp",EDGE,"E17"),sQuery(id+"F1.wireOp",EDGE,"E20")])]});
            var Q38;
            Q38=makeQuery(id+"F2.opExtrude","SWEPT_BODY",BODY,{"disambiguationData":[OSD([sQuery(id+"F1.wireOp",EDGE,"E0.1"),sQuery(id+"F1.wireOp",EDGE,"E13.0.6.0"),sQuery(id+"F1.wireOp",EDGE,"E15"),sQuery(id+"F1.wireOp",EDGE,"E16.1.0.0")])]});
            transform(context, id + "F6", {"entities" : qUnion([Q0, Q1, Q2, Q3, Q4, Q5, Q6, Q7, Q8, Q9, Q10, Q11, Q12, Q13, Q14, Q15, Q16, Q17, Q18, Q19, Q20, Q21, Q22, Q23, Q24, Q25, Q26, Q27, Q28, Q29, Q30, Q31, Q32, Q33, Q34, Q35, Q36, Q37, Q38]), "transformType" : TransformType.TRANSLATION_3D, "dx" : -getVariable(context, 'd'), "dy" : -getVariable(context, 'd'), "dz" : 0 * mm, "makeCopy" : false});
        }
        {
            var Q0;
            Q0=makeQuery(id+"F2.opExtrude","SWEPT_BODY",BODY,{"disambiguationData":[OSD([sQuery(id+"F1.wireOp",EDGE,"E12"),sQuery(id+"F1.wireOp",EDGE,"E13.0.1.0"),sQuery(id+"F1.wireOp",EDGE,"E13.0.2.0"),sQuery(id+"F1.wireOp",EDGE,"E15")])]});
            var Q1;
            Q1=makeQuery(id+"F2.opExtrude","SWEPT_BODY",BODY,{"disambiguationData":[OSD([sQuery(id+"F1.wireOp",EDGE,"E12"),sQuery(id+"F1.wireOp",EDGE,"E13.0.3.0"),sQuery(id+"F1.wireOp",EDGE,"E13.0.4.0"),sQuery(id+"F1.wireOp",EDGE,"E15")])]});
            var Q2;
            Q2=makeQuery(id+"F2.opExtrude","SWEPT_BODY",BODY,{"disambiguationData":[OSD([sQuery(id+"F1.wireOp",EDGE,"E12"),sQuery(id+"F1.wireOp",EDGE,"E13.0.5.0"),sQuery(id+"F1.wireOp",EDGE,"E13.0.6.0"),sQuery(id+"F1.wireOp",EDGE,"E15")])]});
            var Q3;
            Q3=makeQuery(id+"F2.opExtrude","SWEPT_BODY",BODY,{"disambiguationData":[OSD([sQuery(id+"F1.wireOp",EDGE,"E0.1"),sQuery(id+"F1.wireOp",EDGE,"E3"),sQuery(id+"F1.wireOp",EDGE,"E4"),sQuery(id+"F1.wireOp",EDGE,"E6")])]});
            var Q4;
            Q4=makeQuery(id+"F2.opExtrude","SWEPT_BODY",BODY,{"disambiguationData":[OSD([sQuery(id+"F1.wireOp",EDGE,"E3"),sQuery(id+"F1.wireOp",EDGE,"E5"),sQuery(id+"F1.wireOp",EDGE,"E6"),sQuery(id+"F1.wireOp",EDGE,"E19")])]});
            var Q5;
            Q5=makeQuery(id+"F3.opExtrude","SWEPT_BODY",BODY,{"disambiguationData":[OSD([sQuery(id+"F1.wireOp",EDGE,"E3"),sQuery(id+"F1.wireOp",EDGE,"E8"),sQuery(id+"F1.wireOp",EDGE,"E12")])]});
            var Q6;
            Q6=makeQuery(id+"F4.opExtrude","SWEPT_BODY",BODY,{"disambiguationData":[OSD([sQuery(id+"F1.wireOp",EDGE,"E12"),sQuery(id+"F1.wireOp",EDGE,"E13.0.2.0"),sQuery(id+"F1.wireOp",EDGE,"E13.0.3.0"),sQuery(id+"F1.wireOp",EDGE,"E15")])]});
            var Q7;
            Q7=makeQuery(id+"F4.opExtrude","SWEPT_BODY",BODY,{"disambiguationData":[OSD([sQuery(id+"F1.wireOp",EDGE,"E0.1"),sQuery(id+"F1.wireOp",EDGE,"E12"),sQuery(id+"F1.wireOp",EDGE,"E13.0.6.0"),sQuery(id+"F1.wireOp",EDGE,"E15")])]});
            var Q8;
            Q8=makeQuery(id+"F4.opExtrude","SWEPT_BODY",BODY,{"disambiguationData":[OSD([sQuery(id+"F1.wireOp",EDGE,"E12"),sQuery(id+"F1.wireOp",EDGE,"E13.0.4.0"),sQuery(id+"F1.wireOp",EDGE,"E13.0.5.0"),sQuery(id+"F1.wireOp",EDGE,"E15")])]});
            var Q9;
            Q9=makeQuery(id+"F4.opExtrude","SWEPT_BODY",BODY,{"disambiguationData":[OSD([sQuery(id+"F1.wireOp",EDGE,"E2"),sQuery(id+"F1.wireOp",EDGE,"E3"),sQuery(id+"F1.wireOp",EDGE,"E6"),sQuery(id+"F1.wireOp",EDGE,"E19")])]});
            var Q10;
            Q10=makeQuery(id+"F4.opExtrude","SWEPT_BODY",BODY,{"disambiguationData":[OSD([sQuery(id+"F1.wireOp",EDGE,"E3"),sQuery(id+"F1.wireOp",EDGE,"E4"),sQuery(id+"F1.wireOp",EDGE,"E5"),sQuery(id+"F1.wireOp",EDGE,"E6")])]});
            var Q11;
            Q11=makeQuery(id+"F4.opExtrude","SWEPT_BODY",BODY,{"disambiguationData":[OSD([sQuery(id+"F1.wireOp",EDGE,"E1"),sQuery(id+"F1.wireOp",EDGE,"E12"),sQuery(id+"F1.wireOp",EDGE,"E13.0.1.0"),sQuery(id+"F1.wireOp",EDGE,"E15")])]});
            transform(context, id + "F7", {"entities" : qUnion([Q0, Q1, Q2, Q3, Q4, Q5, Q6, Q7, Q8, Q9, Q10, Q11]), "transformType" : TransformType.TRANSLATION_3D, "dx" : 0 * mm, "dy" : -getVariable(context, 'd'), "dz" : 0 * mm, "makeCopy" : false});
        }
        {
            var Q0;
            Q0=makeQuery(id+"F4.opExtrude","SWEPT_BODY",BODY,{"disambiguationData":[OSD([sQuery(id+"F1.wireOp",EDGE,"E3"),sQuery(id+"F1.wireOp",EDGE,"E9"),sQuery(id+"F1.wireOp",EDGE,"E11")])]});
            transform(context, id + "F8", {"entities" : qUnion([Q0]), "transformType" : TransformType.TRANSLATION_3D, "dx" : 0 * mm, "dy" : getVariable(context, 'd'), "dz" : 0 * mm, "makeCopy" : false});
        }
        {
            var Q0;
            Q0=makeQuery(id+"F2.opExtrude","SWEPT_BODY",BODY,{"disambiguationData":[OSD([sQuery(id+"F1.wireOp",EDGE,"E0.2"),sQuery(id+"F1.wireOp",EDGE,"E3"),sQuery(id+"F1.wireOp",EDGE,"E7")])]});
            transform(context, id + "F9", {"entities" : qUnion([Q0]), "transformType" : TransformType.TRANSLATION_3D, "dx" : -getVariable(context, 'd'), "dy" : 0 * mm, "dz" : 0 * mm, "makeCopy" : false});
        }
        {
            var Q0;
            Q0=makeQuery(id+"F3.opExtrude","SWEPT_BODY",BODY,{"disambiguationData":[OSD([sQuery(id+"F1.wireOp",EDGE,"E3"),sQuery(id+"F1.wireOp",EDGE,"E8"),sQuery(id+"F1.wireOp",EDGE,"E12")])]});
            transform(context, id + "F10", {"entities" : qUnion([Q0]), "transformType" : TransformType.TRANSLATION_3D, "dx" : getVariable(context, 'd'), "dy" : 0 * mm, "dz" : 0 * mm, "makeCopy" : false});
        }
        {
            var Q0;
            Q0=makeQuery(id+"F2.opExtrude","SWEPT_BODY",BODY,{"disambiguationData":[OSD([sQuery(id+"F1.wireOp",EDGE,"E0.1"),sQuery(id+"F1.wireOp",EDGE,"E3"),sQuery(id+"F1.wireOp",EDGE,"E4"),sQuery(id+"F1.wireOp",EDGE,"E6")])]});
            var Q1;
            Q1=makeQuery(id+"F2.opExtrude","SWEPT_BODY",BODY,{"disambiguationData":[OSD([sQuery(id+"F1.wireOp",EDGE,"E4"),sQuery(id+"F1.wireOp",EDGE,"E5"),sQuery(id+"F1.wireOp",EDGE,"E6"),sQuery(id+"F1.wireOp",EDGE,"E20")])]});
            var Q2;
            Q2=makeQuery(id+"F3.opExtrude","SWEPT_BODY",BODY,{"disambiguationData":[OSD([sQuery(id+"F1.wireOp",EDGE,"E3"),sQuery(id+"F1.wireOp",EDGE,"E4"),sQuery(id+"F1.wireOp",EDGE,"E5"),sQuery(id+"F1.wireOp",EDGE,"E17")])]});
            var Q3;
            Q3=makeQuery(id+"F4.opExtrude","SWEPT_BODY",BODY,{"disambiguationData":[OSD([sQuery(id+"F1.wireOp",EDGE,"E2"),sQuery(id+"F1.wireOp",EDGE,"E3"),sQuery(id+"F1.wireOp",EDGE,"E6"),sQuery(id+"F1.wireOp",EDGE,"E19")])]});
            var Q4;
            Q4=makeQuery(id+"F4.opExtrude","SWEPT_BODY",BODY,{"disambiguationData":[OSD([sQuery(id+"F1.wireOp",EDGE,"E3"),sQuery(id+"F1.wireOp",EDGE,"E4"),sQuery(id+"F1.wireOp",EDGE,"E5"),sQuery(id+"F1.wireOp",EDGE,"E6")])]});
            var Q5;
            Q5=makeQuery(id+"F2.opExtrude","SWEPT_BODY",BODY,{"disambiguationData":[OSD([sQuery(id+"F1.wireOp",EDGE,"E0.1"),sQuery(id+"F1.wireOp",EDGE,"E4"),sQuery(id+"F1.wireOp",EDGE,"E17"),sQuery(id+"F1.wireOp",EDGE,"E20")])]});
            var Q6;
            Q6=makeQuery(id+"F2.opExtrude","SWEPT_BODY",BODY,{"disambiguationData":[OSD([sQuery(id+"F1.wireOp",EDGE,"E0.1"),sQuery(id+"F1.wireOp",EDGE,"E3"),sQuery(id+"F1.wireOp",EDGE,"E4"),sQuery(id+"F1.wireOp",EDGE,"E18")])]});
            var Q7;
            Q7=makeQuery(id+"F2.opExtrude","SWEPT_BODY",BODY,{"disambiguationData":[OSD([sQuery(id+"F1.wireOp",EDGE,"E3"),sQuery(id+"F1.wireOp",EDGE,"E5"),sQuery(id+"F1.wireOp",EDGE,"E6"),sQuery(id+"F1.wireOp",EDGE,"E19")])]});
            var Q8;
            Q8=makeQuery(id+"F2.opExtrude","SWEPT_BODY",BODY,{"disambiguationData":[OSD([sQuery(id+"F1.wireOp",EDGE,"E3"),sQuery(id+"F1.wireOp",EDGE,"E5"),sQuery(id+"F1.wireOp",EDGE,"E19"),sQuery(id+"F1.wireOp",EDGE,"E20")])]});
            var Q9;
            Q9=makeQuery(id+"F3.opExtrude","SWEPT_BODY",BODY,{"disambiguationData":[OSD([sQuery(id+"F1.wireOp",EDGE,"E2"),sQuery(id+"F1.wireOp",EDGE,"E3"),sQuery(id+"F1.wireOp",EDGE,"E6"),sQuery(id+"F1.wireOp",EDGE,"E19")])]});
            var Q10;
            Q10=makeQuery(id+"F4.opExtrude","SWEPT_BODY",BODY,{"disambiguationData":[OSD([sQuery(id+"F1.wireOp",EDGE,"E5"),sQuery(id+"F1.wireOp",EDGE,"E6"),sQuery(id+"F1.wireOp",EDGE,"E19"),sQuery(id+"F1.wireOp",EDGE,"E20")])]});
            var Q11;
            Q11=makeQuery(id+"F4.opExtrude","SWEPT_BODY",BODY,{"disambiguationData":[OSD([sQuery(id+"F1.wireOp",EDGE,"E4"),sQuery(id+"F1.wireOp",EDGE,"E5"),sQuery(id+"F1.wireOp",EDGE,"E17"),sQuery(id+"F1.wireOp",EDGE,"E20")])]});
            var Q12;
            Q12=makeQuery(id+"F4.opExtrude","SWEPT_BODY",BODY,{"disambiguationData":[OSD([sQuery(id+"F1.wireOp",EDGE,"E0.1"),sQuery(id+"F1.wireOp",EDGE,"E4"),sQuery(id+"F1.wireOp",EDGE,"E17"),sQuery(id+"F1.wireOp",EDGE,"E18")])]});
            var Q13;
            Q13=makeQuery(id+"F4.opExtrude","SWEPT_BODY",BODY,{"disambiguationData":[OSD([sQuery(id+"F1.wireOp",EDGE,"E0.1"),sQuery(id+"F1.wireOp",EDGE,"E4"),sQuery(id+"F1.wireOp",EDGE,"E6"),sQuery(id+"F1.wireOp",EDGE,"E20")])]});
            transform(context, id + "F11", {"entities" : qUnion([Q0, Q1, Q2, Q3, Q4, Q5, Q6, Q7, Q8, Q9, Q10, Q11, Q12, Q13]), "transformType" : TransformType.TRANSLATION_3D, "dx" : 0 * mm, "dy" : -getVariable(context, 'd'), "dz" : 0 * mm, "makeCopy" : false});
        }
        {
            var Q0;
            Q0=makeQuery(id+"F3.opExtrude","SWEPT_BODY",BODY,{"disambiguationData":[OSD([sQuery(id+"F1.wireOp",EDGE,"E3"),sQuery(id+"F1.wireOp",EDGE,"E7"),sQuery(id+"F1.wireOp",EDGE,"E10")])]});
            transform(context, id + "F12", {"entities" : qUnion([Q0]), "transformType" : TransformType.TRANSLATION_3D, "dx" : -getVariable(context, 'd'), "dy" : 0 * mm, "dz" : 0 * mm, "makeCopy" : false});
        }
        {
            var Q0;
            Q0=makeQuery(id+"F2.opExtrude","SWEPT_BODY",BODY,{"disambiguationData":[OSD([sQuery(id+"F1.wireOp",EDGE,"E4"),sQuery(id+"F1.wireOp",EDGE,"E5"),sQuery(id+"F1.wireOp",EDGE,"E6"),sQuery(id+"F1.wireOp",EDGE,"E20")])]});
            var Q1;
            Q1=makeQuery(id+"F2.opExtrude","SWEPT_BODY",BODY,{"disambiguationData":[OSD([sQuery(id+"F1.wireOp",EDGE,"E3"),sQuery(id+"F1.wireOp",EDGE,"E5"),sQuery(id+"F1.wireOp",EDGE,"E6"),sQuery(id+"F1.wireOp",EDGE,"E19")])]});
            var Q2;
            Q2=makeQuery(id+"F4.opExtrude","SWEPT_BODY",BODY,{"disambiguationData":[OSD([sQuery(id+"F1.wireOp",EDGE,"E2"),sQuery(id+"F1.wireOp",EDGE,"E3"),sQuery(id+"F1.wireOp",EDGE,"E6"),sQuery(id+"F1.wireOp",EDGE,"E19")])]});
            var Q3;
            Q3=makeQuery(id+"F4.opExtrude","SWEPT_BODY",BODY,{"disambiguationData":[OSD([sQuery(id+"F1.wireOp",EDGE,"E3"),sQuery(id+"F1.wireOp",EDGE,"E4"),sQuery(id+"F1.wireOp",EDGE,"E5"),sQuery(id+"F1.wireOp",EDGE,"E6")])]});
            var Q4;
            Q4=makeQuery(id+"F3.opExtrude","SWEPT_BODY",BODY,{"disambiguationData":[OSD([sQuery(id+"F1.wireOp",EDGE,"E3"),sQuery(id+"F1.wireOp",EDGE,"E4"),sQuery(id+"F1.wireOp",EDGE,"E5"),sQuery(id+"F1.wireOp",EDGE,"E17")])]});
            var Q5;
            Q5=makeQuery(id+"F2.opExtrude","SWEPT_BODY",BODY,{"disambiguationData":[OSD([sQuery(id+"F1.wireOp",EDGE,"E3"),sQuery(id+"F1.wireOp",EDGE,"E5"),sQuery(id+"F1.wireOp",EDGE,"E19"),sQuery(id+"F1.wireOp",EDGE,"E20")])]});
            var Q6;
            Q6=makeQuery(id+"F3.opExtrude","SWEPT_BODY",BODY,{"disambiguationData":[OSD([sQuery(id+"F1.wireOp",EDGE,"E2"),sQuery(id+"F1.wireOp",EDGE,"E3"),sQuery(id+"F1.wireOp",EDGE,"E6"),sQuery(id+"F1.wireOp",EDGE,"E19")])]});
            var Q7;
            Q7=makeQuery(id+"F4.opExtrude","SWEPT_BODY",BODY,{"disambiguationData":[OSD([sQuery(id+"F1.wireOp",EDGE,"E5"),sQuery(id+"F1.wireOp",EDGE,"E6"),sQuery(id+"F1.wireOp",EDGE,"E19"),sQuery(id+"F1.wireOp",EDGE,"E20")])]});
            var Q8;
            Q8=makeQuery(id+"F4.opExtrude","SWEPT_BODY",BODY,{"disambiguationData":[OSD([sQuery(id+"F1.wireOp",EDGE,"E4"),sQuery(id+"F1.wireOp",EDGE,"E5"),sQuery(id+"F1.wireOp",EDGE,"E17"),sQuery(id+"F1.wireOp",EDGE,"E20")])]});
            transform(context, id + "F13", {"entities" : qUnion([Q0, Q1, Q2, Q3, Q4, Q5, Q6, Q7, Q8]), "transformType" : TransformType.TRANSLATION_3D, "dx" : 0 * mm, "dy" : -getVariable(context, 'd'), "dz" : 0 * mm, "makeCopy" : false});
        }
        {
            var Q0;
            Q0=makeQuery(id+"F2.opExtrude","SWEPT_BODY",BODY,{"disambiguationData":[OSD([sQuery(id+"F1.wireOp",EDGE,"E12"),sQuery(id+"F1.wireOp",EDGE,"E13.0.1.0"),sQuery(id+"F1.wireOp",EDGE,"E13.0.2.0"),sQuery(id+"F1.wireOp",EDGE,"E15")])]});
            var Q1;
            Q1=makeQuery(id+"F2.opExtrude","SWEPT_BODY",BODY,{"disambiguationData":[OSD([sQuery(id+"F1.wireOp",EDGE,"E10"),sQuery(id+"F1.wireOp",EDGE,"E13.0.1.0"),sQuery(id+"F1.wireOp",EDGE,"E13.0.2.0"),sQuery(id+"F1.wireOp",EDGE,"E16.3.0.0")])]});
            var Q2;
            Q2=makeQuery(id+"F2.opExtrude","SWEPT_BODY",BODY,{"disambiguationData":[OSD([sQuery(id+"F1.wireOp",EDGE,"E10"),sQuery(id+"F1.wireOp",EDGE,"E13.0.3.0"),sQuery(id+"F1.wireOp",EDGE,"E13.0.4.0"),sQuery(id+"F1.wireOp",EDGE,"E16.3.0.0")])]});
            var Q3;
            Q3=makeQuery(id+"F2.opExtrude","SWEPT_BODY",BODY,{"disambiguationData":[OSD([sQuery(id+"F1.wireOp",EDGE,"E10"),sQuery(id+"F1.wireOp",EDGE,"E13.0.5.0"),sQuery(id+"F1.wireOp",EDGE,"E13.0.6.0"),sQuery(id+"F1.wireOp",EDGE,"E16.3.0.0")])]});
            var Q4;
            Q4=makeQuery(id+"F2.opExtrude","SWEPT_BODY",BODY,{"disambiguationData":[OSD([sQuery(id+"F1.wireOp",EDGE,"E4"),sQuery(id+"F1.wireOp",EDGE,"E5"),sQuery(id+"F1.wireOp",EDGE,"E6"),sQuery(id+"F1.wireOp",EDGE,"E20")])]});
            var Q5;
            Q5=makeQuery(id+"F2.opExtrude","SWEPT_BODY",BODY,{"disambiguationData":[OSD([sQuery(id+"F1.wireOp",EDGE,"E12"),sQuery(id+"F1.wireOp",EDGE,"E13.0.3.0"),sQuery(id+"F1.wireOp",EDGE,"E13.0.4.0"),sQuery(id+"F1.wireOp",EDGE,"E15")])]});
            var Q6;
            Q6=makeQuery(id+"F2.opExtrude","SWEPT_BODY",BODY,{"disambiguationData":[OSD([sQuery(id+"F1.wireOp",EDGE,"E12"),sQuery(id+"F1.wireOp",EDGE,"E13.0.5.0"),sQuery(id+"F1.wireOp",EDGE,"E13.0.6.0"),sQuery(id+"F1.wireOp",EDGE,"E15")])]});
            var Q7;
            Q7=makeQuery(id+"F2.opExtrude","SWEPT_BODY",BODY,{"disambiguationData":[OSD([sQuery(id+"F1.wireOp",EDGE,"E13.0.1.0"),sQuery(id+"F1.wireOp",EDGE,"E13.0.2.0"),sQuery(id+"F1.wireOp",EDGE,"E16.1.0.0"),sQuery(id+"F1.wireOp",EDGE,"E16.2.0.0")])]});
            var Q8;
            Q8=makeQuery(id+"F2.opExtrude","SWEPT_BODY",BODY,{"disambiguationData":[OSD([sQuery(id+"F1.wireOp",EDGE,"E13.0.2.0"),sQuery(id+"F1.wireOp",EDGE,"E13.0.3.0"),sQuery(id+"F1.wireOp",EDGE,"E15"),sQuery(id+"F1.wireOp",EDGE,"E16.1.0.0")])]});
            var Q9;
            Q9=makeQuery(id+"F2.opExtrude","SWEPT_BODY",BODY,{"disambiguationData":[OSD([sQuery(id+"F1.wireOp",EDGE,"E13.0.2.0"),sQuery(id+"F1.wireOp",EDGE,"E13.0.3.0"),sQuery(id+"F1.wireOp",EDGE,"E16.2.0.0"),sQuery(id+"F1.wireOp",EDGE,"E16.3.0.0")])]});
            var Q10;
            Q10=makeQuery(id+"F2.opExtrude","SWEPT_BODY",BODY,{"disambiguationData":[OSD([sQuery(id+"F1.wireOp",EDGE,"E0.1"),sQuery(id+"F1.wireOp",EDGE,"E3"),sQuery(id+"F1.wireOp",EDGE,"E4"),sQuery(id+"F1.wireOp",EDGE,"E6")])]});
            var Q11;
            Q11=makeQuery(id+"F2.opExtrude","SWEPT_BODY",BODY,{"disambiguationData":[OSD([sQuery(id+"F1.wireOp",EDGE,"E0.1"),sQuery(id+"F1.wireOp",EDGE,"E13.0.6.0"),sQuery(id+"F1.wireOp",EDGE,"E15"),sQuery(id+"F1.wireOp",EDGE,"E16.1.0.0")])]});
            var Q12;
            Q12=makeQuery(id+"F2.opExtrude","SWEPT_BODY",BODY,{"disambiguationData":[OSD([sQuery(id+"F1.wireOp",EDGE,"E0.1"),sQuery(id+"F1.wireOp",EDGE,"E4"),sQuery(id+"F1.wireOp",EDGE,"E17"),sQuery(id+"F1.wireOp",EDGE,"E20")])]});
            var Q13;
            Q13=makeQuery(id+"F2.opExtrude","SWEPT_BODY",BODY,{"disambiguationData":[OSD([sQuery(id+"F1.wireOp",EDGE,"E0.1"),sQuery(id+"F1.wireOp",EDGE,"E13.0.6.0"),sQuery(id+"F1.wireOp",EDGE,"E16.2.0.0"),sQuery(id+"F1.wireOp",EDGE,"E16.3.0.0")])]});
            var Q14;
            Q14=makeQuery(id+"F2.opExtrude","SWEPT_BODY",BODY,{"disambiguationData":[OSD([sQuery(id+"F1.wireOp",EDGE,"E0.1"),sQuery(id+"F1.wireOp",EDGE,"E3"),sQuery(id+"F1.wireOp",EDGE,"E4"),sQuery(id+"F1.wireOp",EDGE,"E18")])]});
            var Q15;
            Q15=makeQuery(id+"F2.opExtrude","SWEPT_BODY",BODY,{"disambiguationData":[OSD([sQuery(id+"F1.wireOp",EDGE,"E3"),sQuery(id+"F1.wireOp",EDGE,"E5"),sQuery(id+"F1.wireOp",EDGE,"E6"),sQuery(id+"F1.wireOp",EDGE,"E19")])]});
            var Q16;
            Q16=makeQuery(id+"F4.opExtrude","SWEPT_BODY",BODY,{"disambiguationData":[OSD([sQuery(id+"F1.wireOp",EDGE,"E2"),sQuery(id+"F1.wireOp",EDGE,"E3"),sQuery(id+"F1.wireOp",EDGE,"E6"),sQuery(id+"F1.wireOp",EDGE,"E19")])]});
            var Q17;
            Q17=makeQuery(id+"F4.opExtrude","SWEPT_BODY",BODY,{"disambiguationData":[OSD([sQuery(id+"F1.wireOp",EDGE,"E3"),sQuery(id+"F1.wireOp",EDGE,"E4"),sQuery(id+"F1.wireOp",EDGE,"E5"),sQuery(id+"F1.wireOp",EDGE,"E6")])]});
            var Q18;
            Q18=makeQuery(id+"F3.opExtrude","SWEPT_BODY",BODY,{"disambiguationData":[OSD([sQuery(id+"F1.wireOp",EDGE,"E3"),sQuery(id+"F1.wireOp",EDGE,"E4"),sQuery(id+"F1.wireOp",EDGE,"E5"),sQuery(id+"F1.wireOp",EDGE,"E17")])]});
            var Q19;
            Q19=makeQuery(id+"F2.opExtrude","SWEPT_BODY",BODY,{"disambiguationData":[OSD([sQuery(id+"F1.wireOp",EDGE,"E13.0.3.0"),sQuery(id+"F1.wireOp",EDGE,"E13.0.4.0"),sQuery(id+"F1.wireOp",EDGE,"E16.1.0.0"),sQuery(id+"F1.wireOp",EDGE,"E16.2.0.0")])]});
            var Q20;
            Q20=makeQuery(id+"F2.opExtrude","SWEPT_BODY",BODY,{"disambiguationData":[OSD([sQuery(id+"F1.wireOp",EDGE,"E13.0.4.0"),sQuery(id+"F1.wireOp",EDGE,"E13.0.5.0"),sQuery(id+"F1.wireOp",EDGE,"E15"),sQuery(id+"F1.wireOp",EDGE,"E16.1.0.0")])]});
            var Q21;
            Q21=makeQuery(id+"F2.opExtrude","SWEPT_BODY",BODY,{"disambiguationData":[OSD([sQuery(id+"F1.wireOp",EDGE,"E13.0.4.0"),sQuery(id+"F1.wireOp",EDGE,"E13.0.5.0"),sQuery(id+"F1.wireOp",EDGE,"E16.2.0.0"),sQuery(id+"F1.wireOp",EDGE,"E16.3.0.0")])]});
            var Q22;
            Q22=makeQuery(id+"F2.opExtrude","SWEPT_BODY",BODY,{"disambiguationData":[OSD([sQuery(id+"F1.wireOp",EDGE,"E13.0.5.0"),sQuery(id+"F1.wireOp",EDGE,"E13.0.6.0"),sQuery(id+"F1.wireOp",EDGE,"E16.1.0.0"),sQuery(id+"F1.wireOp",EDGE,"E16.2.0.0")])]});
            var Q23;
            Q23=makeQuery(id+"F4.opExtrude","SWEPT_BODY",BODY,{"disambiguationData":[OSD([sQuery(id+"F1.wireOp",EDGE,"E12"),sQuery(id+"F1.wireOp",EDGE,"E13.0.2.0"),sQuery(id+"F1.wireOp",EDGE,"E13.0.3.0"),sQuery(id+"F1.wireOp",EDGE,"E15")])]});
            var Q24;
            Q24=makeQuery(id+"F2.opExtrude","SWEPT_BODY",BODY,{"disambiguationData":[OSD([sQuery(id+"F1.wireOp",EDGE,"E3"),sQuery(id+"F1.wireOp",EDGE,"E5"),sQuery(id+"F1.wireOp",EDGE,"E19"),sQuery(id+"F1.wireOp",EDGE,"E20")])]});
            var Q25;
            Q25=makeQuery(id+"F4.opExtrude","SWEPT_BODY",BODY,{"disambiguationData":[OSD([sQuery(id+"F1.wireOp",EDGE,"E0.1"),sQuery(id+"F1.wireOp",EDGE,"E12"),sQuery(id+"F1.wireOp",EDGE,"E13.0.6.0"),sQuery(id+"F1.wireOp",EDGE,"E15")])]});
            var Q26;
            Q26=makeQuery(id+"F3.opExtrude","SWEPT_BODY",BODY,{"disambiguationData":[OSD([sQuery(id+"F1.wireOp",EDGE,"E2"),sQuery(id+"F1.wireOp",EDGE,"E3"),sQuery(id+"F1.wireOp",EDGE,"E6"),sQuery(id+"F1.wireOp",EDGE,"E19")])]});
            var Q27;
            Q27=makeQuery(id+"F4.opExtrude","SWEPT_BODY",BODY,{"disambiguationData":[OSD([sQuery(id+"F1.wireOp",EDGE,"E10"),sQuery(id+"F1.wireOp",EDGE,"E13.0.4.0"),sQuery(id+"F1.wireOp",EDGE,"E13.0.5.0"),sQuery(id+"F1.wireOp",EDGE,"E16.3.0.0")])]});
            var Q28;
            Q28=makeQuery(id+"F4.opExtrude","SWEPT_BODY",BODY,{"disambiguationData":[OSD([sQuery(id+"F1.wireOp",EDGE,"E12"),sQuery(id+"F1.wireOp",EDGE,"E13.0.4.0"),sQuery(id+"F1.wireOp",EDGE,"E13.0.5.0"),sQuery(id+"F1.wireOp",EDGE,"E15")])]});
            var Q29;
            Q29=makeQuery(id+"F4.opExtrude","SWEPT_BODY",BODY,{"disambiguationData":[OSD([sQuery(id+"F1.wireOp",EDGE,"E13.0.5.0"),sQuery(id+"F1.wireOp",EDGE,"E13.0.6.0"),sQuery(id+"F1.wireOp",EDGE,"E16.2.0.0"),sQuery(id+"F1.wireOp",EDGE,"E16.3.0.0")])]});
            var Q30;
            Q30=makeQuery(id+"F4.opExtrude","SWEPT_BODY",BODY,{"disambiguationData":[OSD([sQuery(id+"F1.wireOp",EDGE,"E13.0.5.0"),sQuery(id+"F1.wireOp",EDGE,"E13.0.6.0"),sQuery(id+"F1.wireOp",EDGE,"E15"),sQuery(id+"F1.wireOp",EDGE,"E16.1.0.0")])]});
            var Q31;
            Q31=makeQuery(id+"F4.opExtrude","SWEPT_BODY",BODY,{"disambiguationData":[OSD([sQuery(id+"F1.wireOp",EDGE,"E13.0.4.0"),sQuery(id+"F1.wireOp",EDGE,"E13.0.5.0"),sQuery(id+"F1.wireOp",EDGE,"E16.1.0.0"),sQuery(id+"F1.wireOp",EDGE,"E16.2.0.0")])]});
            var Q32;
            Q32=makeQuery(id+"F4.opExtrude","SWEPT_BODY",BODY,{"disambiguationData":[OSD([sQuery(id+"F1.wireOp",EDGE,"E13.0.3.0"),sQuery(id+"F1.wireOp",EDGE,"E13.0.4.0"),sQuery(id+"F1.wireOp",EDGE,"E16.2.0.0"),sQuery(id+"F1.wireOp",EDGE,"E16.3.0.0")])]});
            var Q33;
            Q33=makeQuery(id+"F4.opExtrude","SWEPT_BODY",BODY,{"disambiguationData":[OSD([sQuery(id+"F1.wireOp",EDGE,"E13.0.3.0"),sQuery(id+"F1.wireOp",EDGE,"E13.0.4.0"),sQuery(id+"F1.wireOp",EDGE,"E15"),sQuery(id+"F1.wireOp",EDGE,"E16.1.0.0")])]});
            var Q34;
            Q34=makeQuery(id+"F4.opExtrude","SWEPT_BODY",BODY,{"disambiguationData":[OSD([sQuery(id+"F1.wireOp",EDGE,"E13.0.2.0"),sQuery(id+"F1.wireOp",EDGE,"E13.0.3.0"),sQuery(id+"F1.wireOp",EDGE,"E16.1.0.0"),sQuery(id+"F1.wireOp",EDGE,"E16.2.0.0")])]});
            var Q35;
            Q35=makeQuery(id+"F4.opExtrude","SWEPT_BODY",BODY,{"disambiguationData":[OSD([sQuery(id+"F1.wireOp",EDGE,"E13.0.1.0"),sQuery(id+"F1.wireOp",EDGE,"E13.0.2.0"),sQuery(id+"F1.wireOp",EDGE,"E16.2.0.0"),sQuery(id+"F1.wireOp",EDGE,"E16.3.0.0")])]});
            var Q36;
            Q36=makeQuery(id+"F4.opExtrude","SWEPT_BODY",BODY,{"disambiguationData":[OSD([sQuery(id+"F1.wireOp",EDGE,"E13.0.1.0"),sQuery(id+"F1.wireOp",EDGE,"E13.0.2.0"),sQuery(id+"F1.wireOp",EDGE,"E15"),sQuery(id+"F1.wireOp",EDGE,"E16.1.0.0")])]});
            var Q37;
            Q37=makeQuery(id+"F4.opExtrude","SWEPT_BODY",BODY,{"disambiguationData":[OSD([sQuery(id+"F1.wireOp",EDGE,"E5"),sQuery(id+"F1.wireOp",EDGE,"E6"),sQuery(id+"F1.wireOp",EDGE,"E19"),sQuery(id+"F1.wireOp",EDGE,"E20")])]});
            var Q38;
            Q38=makeQuery(id+"F4.opExtrude","SWEPT_BODY",BODY,{"disambiguationData":[OSD([sQuery(id+"F1.wireOp",EDGE,"E10"),sQuery(id+"F1.wireOp",EDGE,"E13.0.2.0"),sQuery(id+"F1.wireOp",EDGE,"E13.0.3.0"),sQuery(id+"F1.wireOp",EDGE,"E16.3.0.0")])]});
            var Q39;
            Q39=makeQuery(id+"F4.opExtrude","SWEPT_BODY",BODY,{"disambiguationData":[OSD([sQuery(id+"F1.wireOp",EDGE,"E4"),sQuery(id+"F1.wireOp",EDGE,"E5"),sQuery(id+"F1.wireOp",EDGE,"E17"),sQuery(id+"F1.wireOp",EDGE,"E20")])]});
            var Q40;
            Q40=makeQuery(id+"F4.opExtrude","SWEPT_BODY",BODY,{"disambiguationData":[OSD([sQuery(id+"F1.wireOp",EDGE,"E0.1"),sQuery(id+"F1.wireOp",EDGE,"E10"),sQuery(id+"F1.wireOp",EDGE,"E13.0.6.0"),sQuery(id+"F1.wireOp",EDGE,"E16.3.0.0")])]});
            var Q41;
            Q41=makeQuery(id+"F4.opExtrude","SWEPT_BODY",BODY,{"disambiguationData":[OSD([sQuery(id+"F1.wireOp",EDGE,"E0.1"),sQuery(id+"F1.wireOp",EDGE,"E4"),sQuery(id+"F1.wireOp",EDGE,"E17"),sQuery(id+"F1.wireOp",EDGE,"E18")])]});
            var Q42;
            Q42=makeQuery(id+"F4.opExtrude","SWEPT_BODY",BODY,{"disambiguationData":[OSD([sQuery(id+"F1.wireOp",EDGE,"E0.1"),sQuery(id+"F1.wireOp",EDGE,"E4"),sQuery(id+"F1.wireOp",EDGE,"E6"),sQuery(id+"F1.wireOp",EDGE,"E20")])]});
            var Q43;
            Q43=makeQuery(id+"F4.opExtrude","SWEPT_BODY",BODY,{"disambiguationData":[OSD([sQuery(id+"F1.wireOp",EDGE,"E0.1"),sQuery(id+"F1.wireOp",EDGE,"E13.0.6.0"),sQuery(id+"F1.wireOp",EDGE,"E16.1.0.0"),sQuery(id+"F1.wireOp",EDGE,"E16.2.0.0")])]});
            transform(context, id + "F14", {"entities" : qUnion([Q0, Q1, Q2, Q3, Q4, Q5, Q6, Q7, Q8, Q9, Q10, Q11, Q12, Q13, Q14, Q15, Q16, Q17, Q18, Q19, Q20, Q21, Q22, Q23, Q24, Q25, Q26, Q27, Q28, Q29, Q30, Q31, Q32, Q33, Q34, Q35, Q36, Q37, Q38, Q39, Q40, Q41, Q42, Q43]), "transformType" : TransformType.TRANSLATION_3D, "dx" : 0 * mm, "dy" : -getVariable(context, 'd'), "dz" : 0 * mm, "makeCopy" : false});
        }
        {
            var Q0;
            Q0=makeQuery(id+"F2.opExtrude","SWEPT_BODY",BODY,{"disambiguationData":[OSD([sQuery(id+"F1.wireOp",EDGE,"E10"),sQuery(id+"F1.wireOp",EDGE,"E13.0.1.0"),sQuery(id+"F1.wireOp",EDGE,"E13.0.2.0"),sQuery(id+"F1.wireOp",EDGE,"E16.3.0.0")])]});
            var Q1;
            Q1=makeQuery(id+"F2.opExtrude","SWEPT_BODY",BODY,{"disambiguationData":[OSD([sQuery(id+"F1.wireOp",EDGE,"E10"),sQuery(id+"F1.wireOp",EDGE,"E13.0.3.0"),sQuery(id+"F1.wireOp",EDGE,"E13.0.4.0"),sQuery(id+"F1.wireOp",EDGE,"E16.3.0.0")])]});
            var Q2;
            Q2=makeQuery(id+"F2.opExtrude","SWEPT_BODY",BODY,{"disambiguationData":[OSD([sQuery(id+"F1.wireOp",EDGE,"E10"),sQuery(id+"F1.wireOp",EDGE,"E13.0.5.0"),sQuery(id+"F1.wireOp",EDGE,"E13.0.6.0"),sQuery(id+"F1.wireOp",EDGE,"E16.3.0.0")])]});
            var Q3;
            Q3=makeQuery(id+"F2.opExtrude","SWEPT_BODY",BODY,{"disambiguationData":[OSD([sQuery(id+"F1.wireOp",EDGE,"E13.0.1.0"),sQuery(id+"F1.wireOp",EDGE,"E13.0.2.0"),sQuery(id+"F1.wireOp",EDGE,"E16.1.0.0"),sQuery(id+"F1.wireOp",EDGE,"E16.2.0.0")])]});
            var Q4;
            Q4=makeQuery(id+"F2.opExtrude","SWEPT_BODY",BODY,{"disambiguationData":[OSD([sQuery(id+"F1.wireOp",EDGE,"E13.0.2.0"),sQuery(id+"F1.wireOp",EDGE,"E13.0.3.0"),sQuery(id+"F1.wireOp",EDGE,"E16.2.0.0"),sQuery(id+"F1.wireOp",EDGE,"E16.3.0.0")])]});
            var Q5;
            Q5=makeQuery(id+"F2.opExtrude","SWEPT_BODY",BODY,{"disambiguationData":[OSD([sQuery(id+"F1.wireOp",EDGE,"E0.1"),sQuery(id+"F1.wireOp",EDGE,"E4"),sQuery(id+"F1.wireOp",EDGE,"E17"),sQuery(id+"F1.wireOp",EDGE,"E20")])]});
            var Q6;
            Q6=makeQuery(id+"F2.opExtrude","SWEPT_BODY",BODY,{"disambiguationData":[OSD([sQuery(id+"F1.wireOp",EDGE,"E0.1"),sQuery(id+"F1.wireOp",EDGE,"E13.0.6.0"),sQuery(id+"F1.wireOp",EDGE,"E16.2.0.0"),sQuery(id+"F1.wireOp",EDGE,"E16.3.0.0")])]});
            var Q7;
            Q7=makeQuery(id+"F2.opExtrude","SWEPT_BODY",BODY,{"disambiguationData":[OSD([sQuery(id+"F1.wireOp",EDGE,"E0.1"),sQuery(id+"F1.wireOp",EDGE,"E3"),sQuery(id+"F1.wireOp",EDGE,"E4"),sQuery(id+"F1.wireOp",EDGE,"E18")])]});
            var Q8;
            Q8=makeQuery(id+"F2.opExtrude","SWEPT_BODY",BODY,{"disambiguationData":[OSD([sQuery(id+"F1.wireOp",EDGE,"E1"),sQuery(id+"F1.wireOp",EDGE,"E13.0.1.0"),sQuery(id+"F1.wireOp",EDGE,"E16.2.0.0"),sQuery(id+"F1.wireOp",EDGE,"E16.3.0.0")])]});
            var Q9;
            Q9=makeQuery(id+"F3.opExtrude","SWEPT_BODY",BODY,{"disambiguationData":[OSD([sQuery(id+"F1.wireOp",EDGE,"E3"),sQuery(id+"F1.wireOp",EDGE,"E7"),sQuery(id+"F1.wireOp",EDGE,"E10")])]});
            var Q10;
            Q10=makeQuery(id+"F2.opExtrude","SWEPT_BODY",BODY,{"disambiguationData":[OSD([sQuery(id+"F1.wireOp",EDGE,"E13.0.3.0"),sQuery(id+"F1.wireOp",EDGE,"E13.0.4.0"),sQuery(id+"F1.wireOp",EDGE,"E16.1.0.0"),sQuery(id+"F1.wireOp",EDGE,"E16.2.0.0")])]});
            var Q11;
            Q11=makeQuery(id+"F2.opExtrude","SWEPT_BODY",BODY,{"disambiguationData":[OSD([sQuery(id+"F1.wireOp",EDGE,"E13.0.4.0"),sQuery(id+"F1.wireOp",EDGE,"E13.0.5.0"),sQuery(id+"F1.wireOp",EDGE,"E16.2.0.0"),sQuery(id+"F1.wireOp",EDGE,"E16.3.0.0")])]});
            var Q12;
            Q12=makeQuery(id+"F2.opExtrude","SWEPT_BODY",BODY,{"disambiguationData":[OSD([sQuery(id+"F1.wireOp",EDGE,"E13.0.5.0"),sQuery(id+"F1.wireOp",EDGE,"E13.0.6.0"),sQuery(id+"F1.wireOp",EDGE,"E16.1.0.0"),sQuery(id+"F1.wireOp",EDGE,"E16.2.0.0")])]});
            var Q13;
            Q13=makeQuery(id+"F2.opExtrude","SWEPT_BODY",BODY,{"disambiguationData":[OSD([sQuery(id+"F1.wireOp",EDGE,"E13.0.4.0"),sQuery(id+"F1.wireOp",EDGE,"E13.0.5.0"),sQuery(id+"F1.wireOp",EDGE,"E15"),sQuery(id+"F1.wireOp",EDGE,"E16.1.0.0")])]});
            var Q14;
            Q14=makeQuery(id+"F2.opExtrude","SWEPT_BODY",BODY,{"disambiguationData":[OSD([sQuery(id+"F1.wireOp",EDGE,"E0.1"),sQuery(id+"F1.wireOp",EDGE,"E13.0.6.0"),sQuery(id+"F1.wireOp",EDGE,"E15"),sQuery(id+"F1.wireOp",EDGE,"E16.1.0.0")])]});
            var Q15;
            Q15=makeQuery(id+"F2.opExtrude","SWEPT_BODY",BODY,{"disambiguationData":[OSD([sQuery(id+"F1.wireOp",EDGE,"E3"),sQuery(id+"F1.wireOp",EDGE,"E5"),sQuery(id+"F1.wireOp",EDGE,"E19"),sQuery(id+"F1.wireOp",EDGE,"E20")])]});
            var Q16;
            Q16=makeQuery(id+"F4.opExtrude","SWEPT_BODY",BODY,{"disambiguationData":[OSD([sQuery(id+"F1.wireOp",EDGE,"E10"),sQuery(id+"F1.wireOp",EDGE,"E13.0.4.0"),sQuery(id+"F1.wireOp",EDGE,"E13.0.5.0"),sQuery(id+"F1.wireOp",EDGE,"E16.3.0.0")])]});
            var Q17;
            Q17=makeQuery(id+"F3.opExtrude","SWEPT_BODY",BODY,{"disambiguationData":[OSD([sQuery(id+"F1.wireOp",EDGE,"E3"),sQuery(id+"F1.wireOp",EDGE,"E4"),sQuery(id+"F1.wireOp",EDGE,"E5"),sQuery(id+"F1.wireOp",EDGE,"E17")])]});
            var Q18;
            Q18=makeQuery(id+"F4.opExtrude","SWEPT_BODY",BODY,{"disambiguationData":[OSD([sQuery(id+"F1.wireOp",EDGE,"E13.0.5.0"),sQuery(id+"F1.wireOp",EDGE,"E13.0.6.0"),sQuery(id+"F1.wireOp",EDGE,"E16.2.0.0"),sQuery(id+"F1.wireOp",EDGE,"E16.3.0.0")])]});
            var Q19;
            Q19=makeQuery(id+"F4.opExtrude","SWEPT_BODY",BODY,{"disambiguationData":[OSD([sQuery(id+"F1.wireOp",EDGE,"E13.0.4.0"),sQuery(id+"F1.wireOp",EDGE,"E13.0.5.0"),sQuery(id+"F1.wireOp",EDGE,"E16.1.0.0"),sQuery(id+"F1.wireOp",EDGE,"E16.2.0.0")])]});
            var Q20;
            Q20=makeQuery(id+"F4.opExtrude","SWEPT_BODY",BODY,{"disambiguationData":[OSD([sQuery(id+"F1.wireOp",EDGE,"E13.0.3.0"),sQuery(id+"F1.wireOp",EDGE,"E13.0.4.0"),sQuery(id+"F1.wireOp",EDGE,"E16.2.0.0"),sQuery(id+"F1.wireOp",EDGE,"E16.3.0.0")])]});
            var Q21;
            Q21=makeQuery(id+"F4.opExtrude","SWEPT_BODY",BODY,{"disambiguationData":[OSD([sQuery(id+"F1.wireOp",EDGE,"E13.0.2.0"),sQuery(id+"F1.wireOp",EDGE,"E13.0.3.0"),sQuery(id+"F1.wireOp",EDGE,"E16.1.0.0"),sQuery(id+"F1.wireOp",EDGE,"E16.2.0.0")])]});
            var Q22;
            Q22=makeQuery(id+"F4.opExtrude","SWEPT_BODY",BODY,{"disambiguationData":[OSD([sQuery(id+"F1.wireOp",EDGE,"E13.0.1.0"),sQuery(id+"F1.wireOp",EDGE,"E13.0.2.0"),sQuery(id+"F1.wireOp",EDGE,"E16.2.0.0"),sQuery(id+"F1.wireOp",EDGE,"E16.3.0.0")])]});
            var Q23;
            Q23=makeQuery(id+"F4.opExtrude","SWEPT_BODY",BODY,{"disambiguationData":[OSD([sQuery(id+"F1.wireOp",EDGE,"E10"),sQuery(id+"F1.wireOp",EDGE,"E13.0.2.0"),sQuery(id+"F1.wireOp",EDGE,"E13.0.3.0"),sQuery(id+"F1.wireOp",EDGE,"E16.3.0.0")])]});
            var Q24;
            Q24=makeQuery(id+"F4.opExtrude","SWEPT_BODY",BODY,{"disambiguationData":[OSD([sQuery(id+"F1.wireOp",EDGE,"E4"),sQuery(id+"F1.wireOp",EDGE,"E5"),sQuery(id+"F1.wireOp",EDGE,"E17"),sQuery(id+"F1.wireOp",EDGE,"E20")])]});
            var Q25;
            Q25=makeQuery(id+"F4.opExtrude","SWEPT_BODY",BODY,{"disambiguationData":[OSD([sQuery(id+"F1.wireOp",EDGE,"E1"),sQuery(id+"F1.wireOp",EDGE,"E10"),sQuery(id+"F1.wireOp",EDGE,"E13.0.1.0"),sQuery(id+"F1.wireOp",EDGE,"E16.3.0.0")])]});
            var Q26;
            Q26=makeQuery(id+"F4.opExtrude","SWEPT_BODY",BODY,{"disambiguationData":[OSD([sQuery(id+"F1.wireOp",EDGE,"E1"),sQuery(id+"F1.wireOp",EDGE,"E13.0.1.0"),sQuery(id+"F1.wireOp",EDGE,"E16.1.0.0"),sQuery(id+"F1.wireOp",EDGE,"E16.2.0.0")])]});
            var Q27;
            Q27=makeQuery(id+"F4.opExtrude","SWEPT_BODY",BODY,{"disambiguationData":[OSD([sQuery(id+"F1.wireOp",EDGE,"E0.1"),sQuery(id+"F1.wireOp",EDGE,"E10"),sQuery(id+"F1.wireOp",EDGE,"E13.0.6.0"),sQuery(id+"F1.wireOp",EDGE,"E16.3.0.0")])]});
            var Q28;
            Q28=makeQuery(id+"F4.opExtrude","SWEPT_BODY",BODY,{"disambiguationData":[OSD([sQuery(id+"F1.wireOp",EDGE,"E0.1"),sQuery(id+"F1.wireOp",EDGE,"E4"),sQuery(id+"F1.wireOp",EDGE,"E17"),sQuery(id+"F1.wireOp",EDGE,"E18")])]});
            var Q29;
            Q29=makeQuery(id+"F4.opExtrude","SWEPT_BODY",BODY,{"disambiguationData":[OSD([sQuery(id+"F1.wireOp",EDGE,"E0.1"),sQuery(id+"F1.wireOp",EDGE,"E13.0.6.0"),sQuery(id+"F1.wireOp",EDGE,"E16.1.0.0"),sQuery(id+"F1.wireOp",EDGE,"E16.2.0.0")])]});
            var Q30;
            Q30=makeQuery(id+"F4.opExtrude","SWEPT_BODY",BODY,{"disambiguationData":[OSD([sQuery(id+"F1.wireOp",EDGE,"E13.0.1.0"),sQuery(id+"F1.wireOp",EDGE,"E13.0.2.0"),sQuery(id+"F1.wireOp",EDGE,"E15"),sQuery(id+"F1.wireOp",EDGE,"E16.1.0.0")])]});
            var Q31;
            Q31=makeQuery(id+"F4.opExtrude","SWEPT_BODY",BODY,{"disambiguationData":[OSD([sQuery(id+"F1.wireOp",EDGE,"E13.0.3.0"),sQuery(id+"F1.wireOp",EDGE,"E13.0.4.0"),sQuery(id+"F1.wireOp",EDGE,"E15"),sQuery(id+"F1.wireOp",EDGE,"E16.1.0.0")])]});
            var Q32;
            Q32=makeQuery(id+"F2.opExtrude","SWEPT_BODY",BODY,{"disambiguationData":[OSD([sQuery(id+"F1.wireOp",EDGE,"E13.0.2.0"),sQuery(id+"F1.wireOp",EDGE,"E13.0.3.0"),sQuery(id+"F1.wireOp",EDGE,"E15"),sQuery(id+"F1.wireOp",EDGE,"E16.1.0.0")])]});
            var Q33;
            Q33=makeQuery(id+"F4.opExtrude","SWEPT_BODY",BODY,{"disambiguationData":[OSD([sQuery(id+"F1.wireOp",EDGE,"E13.0.5.0"),sQuery(id+"F1.wireOp",EDGE,"E13.0.6.0"),sQuery(id+"F1.wireOp",EDGE,"E15"),sQuery(id+"F1.wireOp",EDGE,"E16.1.0.0")])]});
            var Q34;
            Q34=makeQuery(id+"F2.opExtrude","SWEPT_BODY",BODY,{"disambiguationData":[OSD([sQuery(id+"F1.wireOp",EDGE,"E4"),sQuery(id+"F1.wireOp",EDGE,"E5"),sQuery(id+"F1.wireOp",EDGE,"E6"),sQuery(id+"F1.wireOp",EDGE,"E20")])]});
            var Q35;
            Q35=makeQuery(id+"F4.opExtrude","SWEPT_BODY",BODY,{"disambiguationData":[OSD([sQuery(id+"F1.wireOp",EDGE,"E5"),sQuery(id+"F1.wireOp",EDGE,"E6"),sQuery(id+"F1.wireOp",EDGE,"E19"),sQuery(id+"F1.wireOp",EDGE,"E20")])]});
            var Q36;
            Q36=makeQuery(id+"F3.opExtrude","SWEPT_BODY",BODY,{"disambiguationData":[OSD([sQuery(id+"F1.wireOp",EDGE,"E2"),sQuery(id+"F1.wireOp",EDGE,"E3"),sQuery(id+"F1.wireOp",EDGE,"E6"),sQuery(id+"F1.wireOp",EDGE,"E19")])]});
            transform(context, id + "F15", {"entities" : qUnion([Q0, Q1, Q2, Q3, Q4, Q5, Q6, Q7, Q8, Q9, Q10, Q11, Q12, Q13, Q14, Q15, Q16, Q17, Q18, Q19, Q20, Q21, Q22, Q23, Q24, Q25, Q26, Q27, Q28, Q29, Q30, Q31, Q32, Q33, Q34, Q35, Q36]), "transformType" : TransformType.TRANSLATION_3D, "dx" : -getVariable(context, 'd'), "dy" : 0 * mm, "dz" : 0 * mm, "makeCopy" : false});
        }
    });
